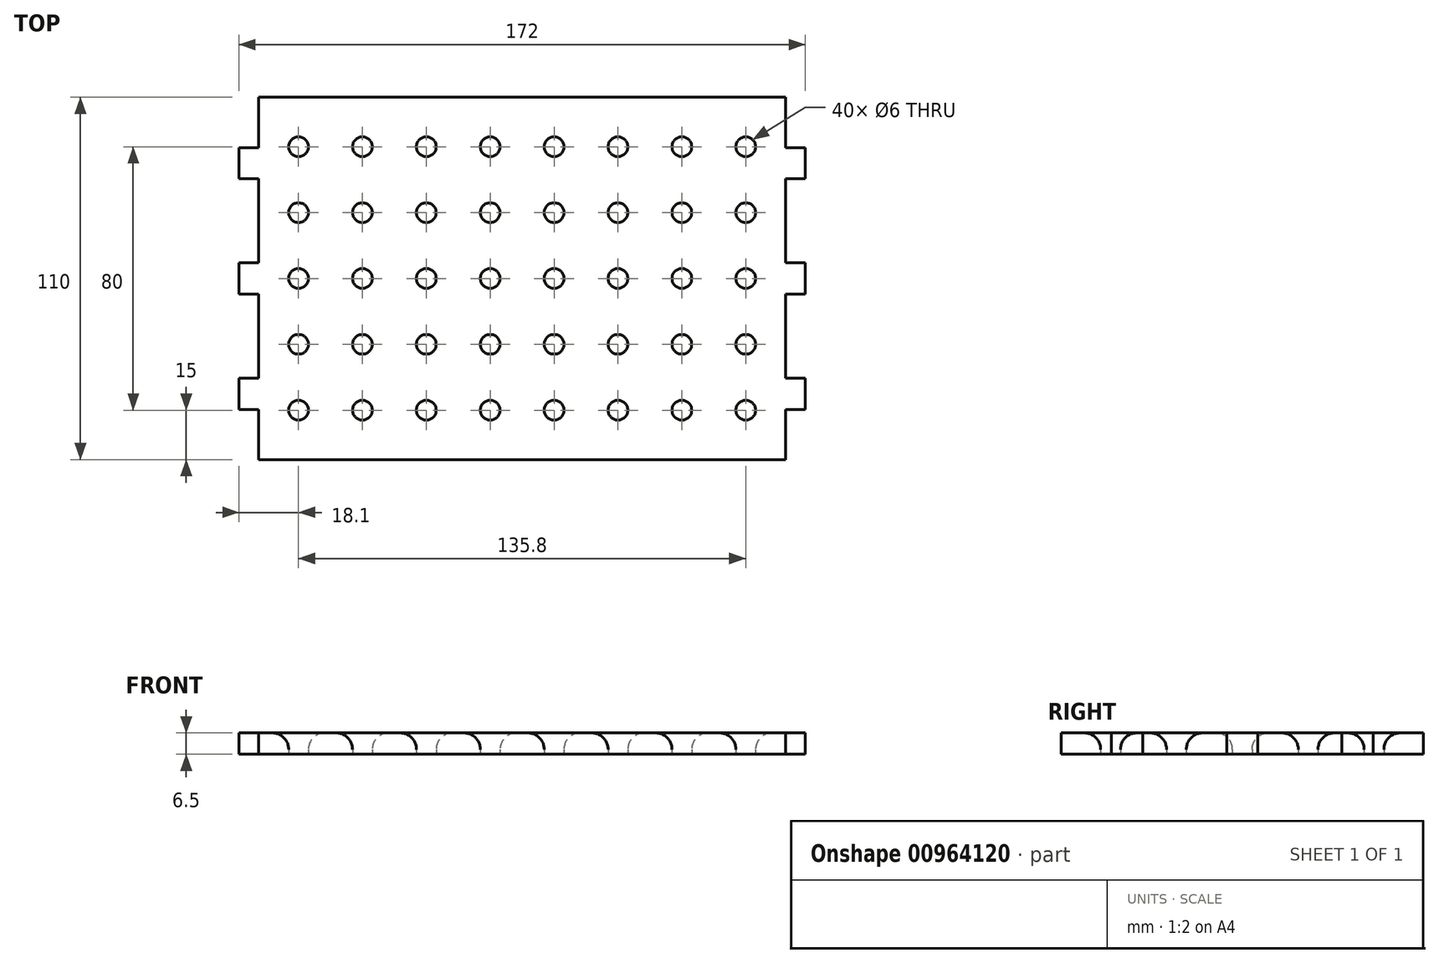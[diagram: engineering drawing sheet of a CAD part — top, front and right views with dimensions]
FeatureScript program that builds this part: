
annotation { "Feature Type Name" : "Feature", "Feature Type Description" : "" }
export const myFeature = defineFeature(function(context is Context, id is Id, definition is map)
    precondition{}
    {
        {
            var Q0;
            Q0=qCreatedBy(makeId("Top.planeOp"),FACE);
            var sketch = newSketch(context, id + "F0", { "sketchPlane" : qUnion([Q0])});
            skLineSegment(sketch, "E0.bottom", {"start": v(-80, 55) * mm, "end": v(80, 55) * mm});
            skLineSegment(sketch, "E0.top", {"start": v(-80, -55) * mm, "end": v(80, -55) * mm});
            skLineSegment(sketch, "E0.left", {"start": v(-80, 55) * mm, "end": v(-80, -55) * mm});
            skLineSegment(sketch, "E0.right", {"start": v(80, 55) * mm, "end": v(80, -55) * mm});
            skPoint(sketch, "E0.middle", {"position": v(0, 0) * mm});
            skSolve(sketch);
        }
        {
            var Q0;
            Q0=makeQuery(id+"F0.imprint","IMPRINT",FACE,{"disambiguationData":[TD([[makeQuery(id+"F0.imprint","IMPRINT",EDGE,{"derivedFrom":sQuery(id+"F0.wireOp",EDGE,"E0.bottom")}),-1.0]])]});
            extrude(context, id + "F1", {"entities" : qUnion([Q0]), "depth" : 6.5 * mm, "offsetDistance" : 25 * mm});
        }
        {
            var Q0;
            Q0=makeQuery(id+"F1.opExtrude","SWEPT_FACE",FACE,{"disambiguationData":[OSD([sQuery(id+"F0.wireOp",EDGE,"E0.left")])]});
            var sketch = newSketch(context, id + "F2", { "sketchPlane" : qUnion([Q0])});
            skLineSegment(sketch, "E1", {"start": v(-55, 3.25) * mm, "end": v(-35, 3.25) * mm});
            skLineSegment(sketch, "E2", {"start": v(-35, 3.25) * mm, "end": v(0, 3.25) * mm});
            skLineSegment(sketch, "E3", {"start": v(0, 3.25) * mm, "end": v(35, 3.25) * mm});
            skLineSegment(sketch, "E4", {"start": v(35, 3.25) * mm, "end": v(55, 3.25) * mm});
            skLineSegment(sketch, "E5.bottom", {"start": v(-39.75, 6.5) * mm, "end": v(-30.25, 6.5) * mm});
            skLineSegment(sketch, "E5.top", {"start": v(-39.75, 0) * mm, "end": v(-30.25, 0) * mm});
            skLineSegment(sketch, "E5.left", {"start": v(-39.75, 6.5) * mm, "end": v(-39.75, 0) * mm});
            skLineSegment(sketch, "E5.right", {"start": v(-30.25, 6.5) * mm, "end": v(-30.25, 0) * mm});
            skPoint(sketch, "E5.middle", {"position": v(-35, 3.25) * mm});
            skLineSegment(sketch, "E6.bottom", {"start": v(-4.75, 6.5) * mm, "end": v(4.75, 6.5) * mm});
            skLineSegment(sketch, "E6.top", {"start": v(-4.75, 0) * mm, "end": v(4.75, 0) * mm});
            skLineSegment(sketch, "E6.left", {"start": v(-4.75, 6.5) * mm, "end": v(-4.75, 0) * mm});
            skLineSegment(sketch, "E6.right", {"start": v(4.75, 6.5) * mm, "end": v(4.75, 0) * mm});
            skPoint(sketch, "E6.middle", {"position": v(0, 3.25) * mm});
            skLineSegment(sketch, "E7.bottom", {"start": v(39.75, 6.5) * mm, "end": v(30.25, 6.5) * mm});
            skLineSegment(sketch, "E7.top", {"start": v(39.75, 0) * mm, "end": v(30.25, 0) * mm});
            skLineSegment(sketch, "E7.left", {"start": v(39.75, 6.5) * mm, "end": v(39.75, 0) * mm});
            skLineSegment(sketch, "E7.right", {"start": v(30.25, 6.5) * mm, "end": v(30.25, 0) * mm});
            skPoint(sketch, "E7.middle", {"position": v(35, 3.25) * mm});
            skSolve(sketch);
        }
        {
            var Q0;
            {var subQ0=sQuery(id+"F2.wireOp",EDGE,"E5.bottom");Q0=makeQuery(id+"F2.imprint","IMPRINT",FACE,{"disambiguationData":[TD([[makeQuery(id+"F2.imprint","IMPRINT",EDGE,{"derivedFrom":subQ0}),-1.0]])]});}
            var Q1;
            {var subQ1=sQuery(id+"F2.wireOp",EDGE,"E5.top");Q1=makeQuery(id+"F2.imprint","IMPRINT",FACE,{"disambiguationData":[TD([[makeQuery(id+"F2.imprint","IMPRINT",EDGE,{"derivedFrom":subQ1}),1.0]])]});}
            var Q2;
            {var subQ1=sQuery(id+"F2.wireOp",EDGE,"E6.bottom");Q2=makeQuery(id+"F2.imprint","IMPRINT",FACE,{"disambiguationData":[TD([[makeQuery(id+"F2.imprint","IMPRINT",EDGE,{"derivedFrom":subQ1}),-1.0]])]});}
            var Q3;
            {var subQ0=sQuery(id+"F2.wireOp",EDGE,"E6.top");Q3=makeQuery(id+"F2.imprint","IMPRINT",FACE,{"disambiguationData":[TD([[makeQuery(id+"F2.imprint","IMPRINT",EDGE,{"derivedFrom":subQ0}),1.0]])]});}
            var Q4;
            {var subQ1=sQuery(id+"F2.wireOp",EDGE,"E7.bottom");Q4=makeQuery(id+"F2.imprint","IMPRINT",FACE,{"disambiguationData":[TD([[makeQuery(id+"F2.imprint","IMPRINT",EDGE,{"derivedFrom":subQ1}),-1.0]])]});}
            var Q5;
            {var subQ1=sQuery(id+"F2.wireOp",EDGE,"E7.top");Q5=makeQuery(id+"F2.imprint","IMPRINT",FACE,{"disambiguationData":[TD([[makeQuery(id+"F2.imprint","IMPRINT",EDGE,{"derivedFrom":subQ1}),1.0]])]});}
            extrude(context, id + "F3", {"entities" : qUnion([Q0, Q1, Q2, Q3, Q4, Q5]), "operationType" : NewBodyOperationType.ADD, "depth" : 6 * mm, "offsetDistance" : 25 * mm});
        }
        {
            var Q0;
            Q0=makeQuery(id+"F1.opExtrude","SWEPT_FACE",FACE,{"disambiguationData":[OSD([sQuery(id+"F0.wireOp",EDGE,"E0.right")])]});
            var sketch = newSketch(context, id + "F4", { "sketchPlane" : qUnion([Q0])});
            skLineSegment(sketch, "E8", {"start": v(-55, 3.25) * mm, "end": v(-35, 3.25) * mm});
            skLineSegment(sketch, "E9", {"start": v(-35, 3.25) * mm, "end": v(0, 3.25) * mm});
            skLineSegment(sketch, "E10", {"start": v(0, 3.25) * mm, "end": v(35, 3.25) * mm});
            skLineSegment(sketch, "E11.bottom", {"start": v(-39.75, 6.5) * mm, "end": v(-30.25, 6.5) * mm});
            skLineSegment(sketch, "E11.top", {"start": v(-39.75, 0) * mm, "end": v(-30.25, 0) * mm});
            skLineSegment(sketch, "E11.left", {"start": v(-39.75, 6.5) * mm, "end": v(-39.75, 0) * mm});
            skLineSegment(sketch, "E11.right", {"start": v(-30.25, 6.5) * mm, "end": v(-30.25, 0) * mm});
            skPoint(sketch, "E11.middle", {"position": v(-35, 3.25) * mm});
            skLineSegment(sketch, "E12.bottom", {"start": v(-4.75, 6.5) * mm, "end": v(4.75, 6.5) * mm});
            skLineSegment(sketch, "E12.top", {"start": v(-4.75, 0) * mm, "end": v(4.75, 0) * mm});
            skLineSegment(sketch, "E12.left", {"start": v(-4.75, 6.5) * mm, "end": v(-4.75, 0) * mm});
            skLineSegment(sketch, "E12.right", {"start": v(4.75, 6.5) * mm, "end": v(4.75, 0) * mm});
            skPoint(sketch, "E12.middle", {"position": v(0, 3.25) * mm});
            skLineSegment(sketch, "E13.bottom", {"start": v(39.75, 6.5) * mm, "end": v(30.25, 6.5) * mm});
            skLineSegment(sketch, "E13.top", {"start": v(39.75, 0) * mm, "end": v(30.25, 0) * mm});
            skLineSegment(sketch, "E13.left", {"start": v(39.75, 6.5) * mm, "end": v(39.75, 0) * mm});
            skLineSegment(sketch, "E13.right", {"start": v(30.25, 6.5) * mm, "end": v(30.25, 0) * mm});
            skPoint(sketch, "E13.middle", {"position": v(35, 3.25) * mm});
            skSolve(sketch);
        }
        {
            var Q0;
            {var subQ1=sQuery(id+"F4.wireOp",EDGE,"E11.bottom");Q0=makeQuery(id+"F4.imprint","IMPRINT",FACE,{"disambiguationData":[TD([[makeQuery(id+"F4.imprint","IMPRINT",EDGE,{"derivedFrom":subQ1}),1.0]])]});}
            var Q1;
            {var subQ1=sQuery(id+"F4.wireOp",EDGE,"E11.top");Q1=makeQuery(id+"F4.imprint","IMPRINT",FACE,{"disambiguationData":[TD([[makeQuery(id+"F4.imprint","IMPRINT",EDGE,{"derivedFrom":subQ1}),-1.0]])]});}
            var Q2;
            {var subQ0=sQuery(id+"F4.wireOp",EDGE,"E12.bottom");Q2=makeQuery(id+"F4.imprint","IMPRINT",FACE,{"disambiguationData":[TD([[makeQuery(id+"F4.imprint","IMPRINT",EDGE,{"derivedFrom":subQ0}),1.0]])]});}
            var Q3;
            {var subQ1=sQuery(id+"F4.wireOp",EDGE,"E12.top");Q3=makeQuery(id+"F4.imprint","IMPRINT",FACE,{"disambiguationData":[TD([[makeQuery(id+"F4.imprint","IMPRINT",EDGE,{"derivedFrom":subQ1}),-1.0]])]});}
            var Q4;
            {var subQ1=sQuery(id+"F4.wireOp",EDGE,"E13.bottom");Q4=makeQuery(id+"F4.imprint","IMPRINT",FACE,{"disambiguationData":[TD([[makeQuery(id+"F4.imprint","IMPRINT",EDGE,{"derivedFrom":subQ1}),1.0]])]});}
            extrude(context, id + "F5", {"entities" : qUnion([Q0, Q1, Q2, Q3, Q4]), "operationType" : NewBodyOperationType.ADD, "depth" : 6 * mm, "offsetDistance" : 25 * mm});
        }
        {
            var Q0;
            Q0=makeQuery(id+"F5.boolean.opBoolean","MERGE",FACE,{"derivedFrom":[makeQuery(id+"F3.boolean.opBoolean","MERGE",FACE,{"derivedFrom":[makeQuery(id+"F1.opExtrude","CAP_FACE",FACE,{"disambiguationData":[OSD([sQuery(id+"F0.wireOp",EDGE,"E0.bottom"),sQuery(id+"F0.wireOp",EDGE,"E0.top"),sQuery(id+"F0.wireOp",EDGE,"E0.left"),sQuery(id+"F0.wireOp",EDGE,"E0.right")])],"isStart":true}),makeQuery(id+"F3.opExtrude","SWEPT_FACE",FACE,{"disambiguationData":[OSD([sQuery(id+"F2.wireOp",EDGE,"E5.top")])]}),makeQuery(id+"F3.opExtrude","SWEPT_FACE",FACE,{"disambiguationData":[OSD([sQuery(id+"F2.wireOp",EDGE,"E6.top")])]}),makeQuery(id+"F3.opExtrude","SWEPT_FACE",FACE,{"disambiguationData":[OSD([sQuery(id+"F2.wireOp",EDGE,"E7.top")])]})]}),makeQuery(id+"F5.opExtrude","SWEPT_FACE",FACE,{"disambiguationData":[OSD([sQuery(id+"F4.wireOp",EDGE,"E11.top")])]}),makeQuery(id+"F5.opExtrude","SWEPT_FACE",FACE,{"disambiguationData":[OSD([sQuery(id+"F4.wireOp",EDGE,"E12.top")])]}),makeQuery(id+"F5.opExtrude","SWEPT_FACE",FACE,{"disambiguationData":[OSD([sQuery(id+"F4.wireOp",EDGE,"E13.top")])]})]});
            var sketch = newSketch(context, id + "F6", { "sketchPlane" : qUnion([Q0])});
            skCircle(sketch, "E14", {"center": v(-67.9, 40) * mm, "radius": 3 * mm});
            skCircle(sketch, "E15", {"center": v(-67.9, 20) * mm, "radius": 3 * mm});
            skCircle(sketch, "E16", {"center": v(-67.9, 0) * mm, "radius": 3 * mm});
            skCircle(sketch, "E17", {"center": v(-67.9, -20) * mm, "radius": 3 * mm});
            skCircle(sketch, "E18", {"center": v(-67.9, -40) * mm, "radius": 3 * mm});
            skCircle(sketch, "E19.1.0.0", {"center": v(-48.5, 40) * mm, "radius": 3 * mm});
            skCircle(sketch, "E19.1.0.1", {"center": v(-48.5, 20) * mm, "radius": 3 * mm});
            skCircle(sketch, "E19.1.0.2", {"center": v(-48.5, 0) * mm, "radius": 3 * mm});
            skCircle(sketch, "E19.1.0.3", {"center": v(-48.5, -20) * mm, "radius": 3 * mm});
            skCircle(sketch, "E19.1.0.4", {"center": v(-48.5, -40) * mm, "radius": 3 * mm});
            skCircle(sketch, "E19.2.0.0", {"center": v(-29.1, 40) * mm, "radius": 3 * mm});
            skCircle(sketch, "E19.2.0.1", {"center": v(-29.1, 20) * mm, "radius": 3 * mm});
            skCircle(sketch, "E19.2.0.2", {"center": v(-29.1, 0) * mm, "radius": 3 * mm});
            skCircle(sketch, "E19.2.0.3", {"center": v(-29.1, -20) * mm, "radius": 3 * mm});
            skCircle(sketch, "E19.2.0.4", {"center": v(-29.1, -40) * mm, "radius": 3 * mm});
            skCircle(sketch, "E19.3.0.0", {"center": v(-9.7, 40) * mm, "radius": 3 * mm});
            skCircle(sketch, "E19.3.0.1", {"center": v(-9.7, 20) * mm, "radius": 3 * mm});
            skCircle(sketch, "E19.3.0.2", {"center": v(-9.7, 0) * mm, "radius": 3 * mm});
            skCircle(sketch, "E19.3.0.3", {"center": v(-9.7, -20) * mm, "radius": 3 * mm});
            skCircle(sketch, "E19.3.0.4", {"center": v(-9.7, -40) * mm, "radius": 3 * mm});
            skCircle(sketch, "E19.4.0.0", {"center": v(9.7, 40) * mm, "radius": 3 * mm});
            skCircle(sketch, "E19.4.0.1", {"center": v(9.7, 20) * mm, "radius": 3 * mm});
            skCircle(sketch, "E19.4.0.2", {"center": v(9.7, 0) * mm, "radius": 3 * mm});
            skCircle(sketch, "E19.4.0.3", {"center": v(9.7, -20) * mm, "radius": 3 * mm});
            skCircle(sketch, "E19.4.0.4", {"center": v(9.7, -40) * mm, "radius": 3 * mm});
            skCircle(sketch, "E19.5.0.0", {"center": v(29.1, 40) * mm, "radius": 3 * mm});
            skCircle(sketch, "E19.5.0.1", {"center": v(29.1, 20) * mm, "radius": 3 * mm});
            skCircle(sketch, "E19.5.0.2", {"center": v(29.1, 0) * mm, "radius": 3 * mm});
            skCircle(sketch, "E19.5.0.3", {"center": v(29.1, -20) * mm, "radius": 3 * mm});
            skCircle(sketch, "E19.5.0.4", {"center": v(29.1, -40) * mm, "radius": 3 * mm});
            skCircle(sketch, "E19.6.0.0", {"center": v(48.5, 40) * mm, "radius": 3 * mm});
            skCircle(sketch, "E19.6.0.1", {"center": v(48.5, 20) * mm, "radius": 3 * mm});
            skCircle(sketch, "E19.6.0.2", {"center": v(48.5, 0) * mm, "radius": 3 * mm});
            skCircle(sketch, "E19.6.0.3", {"center": v(48.5, -20) * mm, "radius": 3 * mm});
            skCircle(sketch, "E19.6.0.4", {"center": v(48.5, -40) * mm, "radius": 3 * mm});
            skCircle(sketch, "E19.7.0.0", {"center": v(67.9, 40) * mm, "radius": 3 * mm});
            skCircle(sketch, "E19.7.0.1", {"center": v(67.9, 20) * mm, "radius": 3 * mm});
            skCircle(sketch, "E19.7.0.2", {"center": v(67.9, 0) * mm, "radius": 3 * mm});
            skCircle(sketch, "E19.7.0.3", {"center": v(67.9, -20) * mm, "radius": 3 * mm});
            skCircle(sketch, "E19.7.0.4", {"center": v(67.9, -40) * mm, "radius": 3 * mm});
            skLineSegment(sketch, "E19.direction1", {"start": v(-67.9, 40) * mm, "end": v(-48.5, 40) * mm, "construction": true});
            skSolve(sketch);
        }
        {
            var Q0;
            Q0=makeQuery(id+"F6.imprint","IMPRINT",FACE,{"disambiguationData":[TD([[makeQuery(id+"F6.imprint","IMPRINT",EDGE,{"derivedFrom":sQuery(id+"F6.wireOp",EDGE,"E14")}),1.0]])]});
            var Q1;
            Q1=makeQuery(id+"F6.imprint","IMPRINT",FACE,{"disambiguationData":[TD([[makeQuery(id+"F6.imprint","IMPRINT",EDGE,{"derivedFrom":sQuery(id+"F6.wireOp",EDGE,"E19.1.0.0")}),1.0]])]});
            var Q2;
            Q2=makeQuery(id+"F6.imprint","IMPRINT",FACE,{"disambiguationData":[TD([[makeQuery(id+"F6.imprint","IMPRINT",EDGE,{"derivedFrom":sQuery(id+"F6.wireOp",EDGE,"E19.2.0.0")}),1.0]])]});
            var Q3;
            Q3=makeQuery(id+"F6.imprint","IMPRINT",FACE,{"disambiguationData":[TD([[makeQuery(id+"F6.imprint","IMPRINT",EDGE,{"derivedFrom":sQuery(id+"F6.wireOp",EDGE,"E19.3.0.0")}),1.0]])]});
            var Q4;
            Q4=makeQuery(id+"F6.imprint","IMPRINT",FACE,{"disambiguationData":[TD([[makeQuery(id+"F6.imprint","IMPRINT",EDGE,{"derivedFrom":sQuery(id+"F6.wireOp",EDGE,"E19.4.0.0")}),1.0]])]});
            var Q5;
            Q5=makeQuery(id+"F6.imprint","IMPRINT",FACE,{"disambiguationData":[TD([[makeQuery(id+"F6.imprint","IMPRINT",EDGE,{"derivedFrom":sQuery(id+"F6.wireOp",EDGE,"E19.5.0.0")}),1.0]])]});
            var Q6;
            Q6=makeQuery(id+"F6.imprint","IMPRINT",FACE,{"disambiguationData":[TD([[makeQuery(id+"F6.imprint","IMPRINT",EDGE,{"derivedFrom":sQuery(id+"F6.wireOp",EDGE,"E19.6.0.0")}),1.0]])]});
            var Q7;
            Q7=makeQuery(id+"F6.imprint","IMPRINT",FACE,{"disambiguationData":[TD([[makeQuery(id+"F6.imprint","IMPRINT",EDGE,{"derivedFrom":sQuery(id+"F6.wireOp",EDGE,"E19.7.0.0")}),1.0]])]});
            var Q8;
            Q8=makeQuery(id+"F6.imprint","IMPRINT",FACE,{"disambiguationData":[TD([[makeQuery(id+"F6.imprint","IMPRINT",EDGE,{"derivedFrom":sQuery(id+"F6.wireOp",EDGE,"E19.7.0.1")}),1.0]])]});
            var Q9;
            Q9=makeQuery(id+"F6.imprint","IMPRINT",FACE,{"disambiguationData":[TD([[makeQuery(id+"F6.imprint","IMPRINT",EDGE,{"derivedFrom":sQuery(id+"F6.wireOp",EDGE,"E19.6.0.1")}),1.0]])]});
            var Q10;
            Q10=makeQuery(id+"F6.imprint","IMPRINT",FACE,{"disambiguationData":[TD([[makeQuery(id+"F6.imprint","IMPRINT",EDGE,{"derivedFrom":sQuery(id+"F6.wireOp",EDGE,"E19.5.0.1")}),1.0]])]});
            var Q11;
            Q11=makeQuery(id+"F6.imprint","IMPRINT",FACE,{"disambiguationData":[TD([[makeQuery(id+"F6.imprint","IMPRINT",EDGE,{"derivedFrom":sQuery(id+"F6.wireOp",EDGE,"E19.4.0.1")}),1.0]])]});
            var Q12;
            Q12=makeQuery(id+"F6.imprint","IMPRINT",FACE,{"disambiguationData":[TD([[makeQuery(id+"F6.imprint","IMPRINT",EDGE,{"derivedFrom":sQuery(id+"F6.wireOp",EDGE,"E19.3.0.1")}),1.0]])]});
            var Q13;
            Q13=makeQuery(id+"F6.imprint","IMPRINT",FACE,{"disambiguationData":[TD([[makeQuery(id+"F6.imprint","IMPRINT",EDGE,{"derivedFrom":sQuery(id+"F6.wireOp",EDGE,"E19.2.0.1")}),1.0]])]});
            var Q14;
            Q14=makeQuery(id+"F6.imprint","IMPRINT",FACE,{"disambiguationData":[TD([[makeQuery(id+"F6.imprint","IMPRINT",EDGE,{"derivedFrom":sQuery(id+"F6.wireOp",EDGE,"E19.1.0.1")}),1.0]])]});
            var Q15;
            Q15=makeQuery(id+"F6.imprint","IMPRINT",FACE,{"disambiguationData":[TD([[makeQuery(id+"F6.imprint","IMPRINT",EDGE,{"derivedFrom":sQuery(id+"F6.wireOp",EDGE,"E15")}),1.0]])]});
            var Q16;
            Q16=makeQuery(id+"F6.imprint","IMPRINT",FACE,{"disambiguationData":[TD([[makeQuery(id+"F6.imprint","IMPRINT",EDGE,{"derivedFrom":sQuery(id+"F6.wireOp",EDGE,"E16")}),1.0]])]});
            var Q17;
            Q17=makeQuery(id+"F6.imprint","IMPRINT",FACE,{"disambiguationData":[TD([[makeQuery(id+"F6.imprint","IMPRINT",EDGE,{"derivedFrom":sQuery(id+"F6.wireOp",EDGE,"E19.1.0.2")}),1.0]])]});
            var Q18;
            Q18=makeQuery(id+"F6.imprint","IMPRINT",FACE,{"disambiguationData":[TD([[makeQuery(id+"F6.imprint","IMPRINT",EDGE,{"derivedFrom":sQuery(id+"F6.wireOp",EDGE,"E19.2.0.2")}),1.0]])]});
            var Q19;
            Q19=makeQuery(id+"F6.imprint","IMPRINT",FACE,{"disambiguationData":[TD([[makeQuery(id+"F6.imprint","IMPRINT",EDGE,{"derivedFrom":sQuery(id+"F6.wireOp",EDGE,"E19.3.0.2")}),1.0]])]});
            var Q20;
            Q20=makeQuery(id+"F6.imprint","IMPRINT",FACE,{"disambiguationData":[TD([[makeQuery(id+"F6.imprint","IMPRINT",EDGE,{"derivedFrom":sQuery(id+"F6.wireOp",EDGE,"E19.4.0.2")}),1.0]])]});
            var Q21;
            Q21=makeQuery(id+"F6.imprint","IMPRINT",FACE,{"disambiguationData":[TD([[makeQuery(id+"F6.imprint","IMPRINT",EDGE,{"derivedFrom":sQuery(id+"F6.wireOp",EDGE,"E19.5.0.2")}),1.0]])]});
            var Q22;
            Q22=makeQuery(id+"F6.imprint","IMPRINT",FACE,{"disambiguationData":[TD([[makeQuery(id+"F6.imprint","IMPRINT",EDGE,{"derivedFrom":sQuery(id+"F6.wireOp",EDGE,"E19.6.0.2")}),1.0]])]});
            var Q23;
            Q23=makeQuery(id+"F6.imprint","IMPRINT",FACE,{"disambiguationData":[TD([[makeQuery(id+"F6.imprint","IMPRINT",EDGE,{"derivedFrom":sQuery(id+"F6.wireOp",EDGE,"E19.7.0.2")}),1.0]])]});
            var Q24;
            Q24=makeQuery(id+"F6.imprint","IMPRINT",FACE,{"disambiguationData":[TD([[makeQuery(id+"F6.imprint","IMPRINT",EDGE,{"derivedFrom":sQuery(id+"F6.wireOp",EDGE,"E19.7.0.3")}),1.0]])]});
            var Q25;
            Q25=makeQuery(id+"F6.imprint","IMPRINT",FACE,{"disambiguationData":[TD([[makeQuery(id+"F6.imprint","IMPRINT",EDGE,{"derivedFrom":sQuery(id+"F6.wireOp",EDGE,"E19.6.0.3")}),1.0]])]});
            var Q26;
            Q26=makeQuery(id+"F6.imprint","IMPRINT",FACE,{"disambiguationData":[TD([[makeQuery(id+"F6.imprint","IMPRINT",EDGE,{"derivedFrom":sQuery(id+"F6.wireOp",EDGE,"E19.5.0.3")}),1.0]])]});
            var Q27;
            Q27=makeQuery(id+"F6.imprint","IMPRINT",FACE,{"disambiguationData":[TD([[makeQuery(id+"F6.imprint","IMPRINT",EDGE,{"derivedFrom":sQuery(id+"F6.wireOp",EDGE,"E19.4.0.3")}),1.0]])]});
            var Q28;
            Q28=makeQuery(id+"F6.imprint","IMPRINT",FACE,{"disambiguationData":[TD([[makeQuery(id+"F6.imprint","IMPRINT",EDGE,{"derivedFrom":sQuery(id+"F6.wireOp",EDGE,"E19.3.0.3")}),1.0]])]});
            var Q29;
            Q29=makeQuery(id+"F6.imprint","IMPRINT",FACE,{"disambiguationData":[TD([[makeQuery(id+"F6.imprint","IMPRINT",EDGE,{"derivedFrom":sQuery(id+"F6.wireOp",EDGE,"E19.2.0.3")}),1.0]])]});
            var Q30;
            Q30=makeQuery(id+"F6.imprint","IMPRINT",FACE,{"disambiguationData":[TD([[makeQuery(id+"F6.imprint","IMPRINT",EDGE,{"derivedFrom":sQuery(id+"F6.wireOp",EDGE,"E19.1.0.3")}),1.0]])]});
            var Q31;
            Q31=makeQuery(id+"F6.imprint","IMPRINT",FACE,{"disambiguationData":[TD([[makeQuery(id+"F6.imprint","IMPRINT",EDGE,{"derivedFrom":sQuery(id+"F6.wireOp",EDGE,"E17")}),1.0]])]});
            var Q32;
            Q32=makeQuery(id+"F6.imprint","IMPRINT",FACE,{"disambiguationData":[TD([[makeQuery(id+"F6.imprint","IMPRINT",EDGE,{"derivedFrom":sQuery(id+"F6.wireOp",EDGE,"E18")}),1.0]])]});
            var Q33;
            Q33=makeQuery(id+"F6.imprint","IMPRINT",FACE,{"disambiguationData":[TD([[makeQuery(id+"F6.imprint","IMPRINT",EDGE,{"derivedFrom":sQuery(id+"F6.wireOp",EDGE,"E19.1.0.4")}),1.0]])]});
            var Q34;
            Q34=makeQuery(id+"F6.imprint","IMPRINT",FACE,{"disambiguationData":[TD([[makeQuery(id+"F6.imprint","IMPRINT",EDGE,{"derivedFrom":sQuery(id+"F6.wireOp",EDGE,"E19.2.0.4")}),1.0]])]});
            var Q35;
            Q35=makeQuery(id+"F6.imprint","IMPRINT",FACE,{"disambiguationData":[TD([[makeQuery(id+"F6.imprint","IMPRINT",EDGE,{"derivedFrom":sQuery(id+"F6.wireOp",EDGE,"E19.3.0.4")}),1.0]])]});
            var Q36;
            Q36=makeQuery(id+"F6.imprint","IMPRINT",FACE,{"disambiguationData":[TD([[makeQuery(id+"F6.imprint","IMPRINT",EDGE,{"derivedFrom":sQuery(id+"F6.wireOp",EDGE,"E19.4.0.4")}),1.0]])]});
            var Q37;
            Q37=makeQuery(id+"F6.imprint","IMPRINT",FACE,{"disambiguationData":[TD([[makeQuery(id+"F6.imprint","IMPRINT",EDGE,{"derivedFrom":sQuery(id+"F6.wireOp",EDGE,"E19.5.0.4")}),1.0]])]});
            var Q38;
            Q38=makeQuery(id+"F6.imprint","IMPRINT",FACE,{"disambiguationData":[TD([[makeQuery(id+"F6.imprint","IMPRINT",EDGE,{"derivedFrom":sQuery(id+"F6.wireOp",EDGE,"E19.6.0.4")}),1.0]])]});
            var Q39;
            Q39=makeQuery(id+"F6.imprint","IMPRINT",FACE,{"disambiguationData":[TD([[makeQuery(id+"F6.imprint","IMPRINT",EDGE,{"derivedFrom":sQuery(id+"F6.wireOp",EDGE,"E19.7.0.4")}),1.0]])]});
            extrude(context, id + "F7", {"entities" : qUnion([Q0, Q1, Q2, Q3, Q4, Q5, Q6, Q7, Q8, Q9, Q10, Q11, Q12, Q13, Q14, Q15, Q16, Q17, Q18, Q19, Q20, Q21, Q22, Q23, Q24, Q25, Q26, Q27, Q28, Q29, Q30, Q31, Q32, Q33, Q34, Q35, Q36, Q37, Q38, Q39]), "operationType" : NewBodyOperationType.REMOVE, "oppositeDirection" : true, "depth" : 25 * mm, "offsetDistance" : 25 * mm});
        }
        {
            var Q0;
            Q0=makeQuery(id+"F7.boolean.opBoolean","INTERSECT",EDGE,{"derivedFrom":[makeQuery(id+"F5.boolean.opBoolean","MERGE",FACE,{"derivedFrom":[makeQuery(id+"F3.boolean.opBoolean","MERGE",FACE,{"derivedFrom":[makeQuery(id+"F1.opExtrude","CAP_FACE",FACE,{"disambiguationData":[OSD([sQuery(id+"F0.wireOp",EDGE,"E0.bottom"),sQuery(id+"F0.wireOp",EDGE,"E0.top"),sQuery(id+"F0.wireOp",EDGE,"E0.left"),sQuery(id+"F0.wireOp",EDGE,"E0.right")])],"isStart":false}),makeQuery(id+"F3.opExtrude","SWEPT_FACE",FACE,{"disambiguationData":[OSD([sQuery(id+"F2.wireOp",EDGE,"E5.bottom")])]}),makeQuery(id+"F3.opExtrude","SWEPT_FACE",FACE,{"disambiguationData":[OSD([sQuery(id+"F2.wireOp",EDGE,"E6.bottom")])]}),makeQuery(id+"F3.opExtrude","SWEPT_FACE",FACE,{"disambiguationData":[OSD([sQuery(id+"F2.wireOp",EDGE,"E7.bottom")])]})]}),makeQuery(id+"F5.opExtrude","SWEPT_FACE",FACE,{"disambiguationData":[OSD([sQuery(id+"F4.wireOp",EDGE,"E11.bottom")])]}),makeQuery(id+"F5.opExtrude","SWEPT_FACE",FACE,{"disambiguationData":[OSD([sQuery(id+"F4.wireOp",EDGE,"E12.bottom")])]}),makeQuery(id+"F5.opExtrude","SWEPT_FACE",FACE,{"disambiguationData":[OSD([sQuery(id+"F4.wireOp",EDGE,"E13.bottom")])]})]}),makeQuery(id+"F7.opExtrude","SWEPT_FACE",FACE,{"disambiguationData":[OSD([sQuery(id+"F6.wireOp",EDGE,"E18")])]})]});
            var Q1;
            Q1=makeQuery(id+"F7.boolean.opBoolean","INTERSECT",EDGE,{"derivedFrom":[makeQuery(id+"F5.boolean.opBoolean","MERGE",FACE,{"derivedFrom":[makeQuery(id+"F3.boolean.opBoolean","MERGE",FACE,{"derivedFrom":[makeQuery(id+"F1.opExtrude","CAP_FACE",FACE,{"disambiguationData":[OSD([sQuery(id+"F0.wireOp",EDGE,"E0.bottom"),sQuery(id+"F0.wireOp",EDGE,"E0.top"),sQuery(id+"F0.wireOp",EDGE,"E0.left"),sQuery(id+"F0.wireOp",EDGE,"E0.right")])],"isStart":false}),makeQuery(id+"F3.opExtrude","SWEPT_FACE",FACE,{"disambiguationData":[OSD([sQuery(id+"F2.wireOp",EDGE,"E5.bottom")])]}),makeQuery(id+"F3.opExtrude","SWEPT_FACE",FACE,{"disambiguationData":[OSD([sQuery(id+"F2.wireOp",EDGE,"E6.bottom")])]}),makeQuery(id+"F3.opExtrude","SWEPT_FACE",FACE,{"disambiguationData":[OSD([sQuery(id+"F2.wireOp",EDGE,"E7.bottom")])]})]}),makeQuery(id+"F5.opExtrude","SWEPT_FACE",FACE,{"disambiguationData":[OSD([sQuery(id+"F4.wireOp",EDGE,"E11.bottom")])]}),makeQuery(id+"F5.opExtrude","SWEPT_FACE",FACE,{"disambiguationData":[OSD([sQuery(id+"F4.wireOp",EDGE,"E12.bottom")])]}),makeQuery(id+"F5.opExtrude","SWEPT_FACE",FACE,{"disambiguationData":[OSD([sQuery(id+"F4.wireOp",EDGE,"E13.bottom")])]})]}),makeQuery(id+"F7.opExtrude","SWEPT_FACE",FACE,{"disambiguationData":[OSD([sQuery(id+"F6.wireOp",EDGE,"E19.1.0.4")])]})]});
            var Q2;
            Q2=makeQuery(id+"F7.boolean.opBoolean","INTERSECT",EDGE,{"derivedFrom":[makeQuery(id+"F5.boolean.opBoolean","MERGE",FACE,{"derivedFrom":[makeQuery(id+"F3.boolean.opBoolean","MERGE",FACE,{"derivedFrom":[makeQuery(id+"F1.opExtrude","CAP_FACE",FACE,{"disambiguationData":[OSD([sQuery(id+"F0.wireOp",EDGE,"E0.bottom"),sQuery(id+"F0.wireOp",EDGE,"E0.top"),sQuery(id+"F0.wireOp",EDGE,"E0.left"),sQuery(id+"F0.wireOp",EDGE,"E0.right")])],"isStart":false}),makeQuery(id+"F3.opExtrude","SWEPT_FACE",FACE,{"disambiguationData":[OSD([sQuery(id+"F2.wireOp",EDGE,"E5.bottom")])]}),makeQuery(id+"F3.opExtrude","SWEPT_FACE",FACE,{"disambiguationData":[OSD([sQuery(id+"F2.wireOp",EDGE,"E6.bottom")])]}),makeQuery(id+"F3.opExtrude","SWEPT_FACE",FACE,{"disambiguationData":[OSD([sQuery(id+"F2.wireOp",EDGE,"E7.bottom")])]})]}),makeQuery(id+"F5.opExtrude","SWEPT_FACE",FACE,{"disambiguationData":[OSD([sQuery(id+"F4.wireOp",EDGE,"E11.bottom")])]}),makeQuery(id+"F5.opExtrude","SWEPT_FACE",FACE,{"disambiguationData":[OSD([sQuery(id+"F4.wireOp",EDGE,"E12.bottom")])]}),makeQuery(id+"F5.opExtrude","SWEPT_FACE",FACE,{"disambiguationData":[OSD([sQuery(id+"F4.wireOp",EDGE,"E13.bottom")])]})]}),makeQuery(id+"F7.opExtrude","SWEPT_FACE",FACE,{"disambiguationData":[OSD([sQuery(id+"F6.wireOp",EDGE,"E19.2.0.4")])]})]});
            var Q3;
            Q3=makeQuery(id+"F7.boolean.opBoolean","INTERSECT",EDGE,{"derivedFrom":[makeQuery(id+"F5.boolean.opBoolean","MERGE",FACE,{"derivedFrom":[makeQuery(id+"F3.boolean.opBoolean","MERGE",FACE,{"derivedFrom":[makeQuery(id+"F1.opExtrude","CAP_FACE",FACE,{"disambiguationData":[OSD([sQuery(id+"F0.wireOp",EDGE,"E0.bottom"),sQuery(id+"F0.wireOp",EDGE,"E0.top"),sQuery(id+"F0.wireOp",EDGE,"E0.left"),sQuery(id+"F0.wireOp",EDGE,"E0.right")])],"isStart":false}),makeQuery(id+"F3.opExtrude","SWEPT_FACE",FACE,{"disambiguationData":[OSD([sQuery(id+"F2.wireOp",EDGE,"E5.bottom")])]}),makeQuery(id+"F3.opExtrude","SWEPT_FACE",FACE,{"disambiguationData":[OSD([sQuery(id+"F2.wireOp",EDGE,"E6.bottom")])]}),makeQuery(id+"F3.opExtrude","SWEPT_FACE",FACE,{"disambiguationData":[OSD([sQuery(id+"F2.wireOp",EDGE,"E7.bottom")])]})]}),makeQuery(id+"F5.opExtrude","SWEPT_FACE",FACE,{"disambiguationData":[OSD([sQuery(id+"F4.wireOp",EDGE,"E11.bottom")])]}),makeQuery(id+"F5.opExtrude","SWEPT_FACE",FACE,{"disambiguationData":[OSD([sQuery(id+"F4.wireOp",EDGE,"E12.bottom")])]}),makeQuery(id+"F5.opExtrude","SWEPT_FACE",FACE,{"disambiguationData":[OSD([sQuery(id+"F4.wireOp",EDGE,"E13.bottom")])]})]}),makeQuery(id+"F7.opExtrude","SWEPT_FACE",FACE,{"disambiguationData":[OSD([sQuery(id+"F6.wireOp",EDGE,"E19.3.0.4")])]})]});
            var Q4;
            Q4=makeQuery(id+"F7.boolean.opBoolean","INTERSECT",EDGE,{"derivedFrom":[makeQuery(id+"F5.boolean.opBoolean","MERGE",FACE,{"derivedFrom":[makeQuery(id+"F3.boolean.opBoolean","MERGE",FACE,{"derivedFrom":[makeQuery(id+"F1.opExtrude","CAP_FACE",FACE,{"disambiguationData":[OSD([sQuery(id+"F0.wireOp",EDGE,"E0.bottom"),sQuery(id+"F0.wireOp",EDGE,"E0.top"),sQuery(id+"F0.wireOp",EDGE,"E0.left"),sQuery(id+"F0.wireOp",EDGE,"E0.right")])],"isStart":false}),makeQuery(id+"F3.opExtrude","SWEPT_FACE",FACE,{"disambiguationData":[OSD([sQuery(id+"F2.wireOp",EDGE,"E5.bottom")])]}),makeQuery(id+"F3.opExtrude","SWEPT_FACE",FACE,{"disambiguationData":[OSD([sQuery(id+"F2.wireOp",EDGE,"E6.bottom")])]}),makeQuery(id+"F3.opExtrude","SWEPT_FACE",FACE,{"disambiguationData":[OSD([sQuery(id+"F2.wireOp",EDGE,"E7.bottom")])]})]}),makeQuery(id+"F5.opExtrude","SWEPT_FACE",FACE,{"disambiguationData":[OSD([sQuery(id+"F4.wireOp",EDGE,"E11.bottom")])]}),makeQuery(id+"F5.opExtrude","SWEPT_FACE",FACE,{"disambiguationData":[OSD([sQuery(id+"F4.wireOp",EDGE,"E12.bottom")])]}),makeQuery(id+"F5.opExtrude","SWEPT_FACE",FACE,{"disambiguationData":[OSD([sQuery(id+"F4.wireOp",EDGE,"E13.bottom")])]})]}),makeQuery(id+"F7.opExtrude","SWEPT_FACE",FACE,{"disambiguationData":[OSD([sQuery(id+"F6.wireOp",EDGE,"E19.4.0.4")])]})]});
            var Q5;
            Q5=makeQuery(id+"F7.boolean.opBoolean","INTERSECT",EDGE,{"derivedFrom":[makeQuery(id+"F5.boolean.opBoolean","MERGE",FACE,{"derivedFrom":[makeQuery(id+"F3.boolean.opBoolean","MERGE",FACE,{"derivedFrom":[makeQuery(id+"F1.opExtrude","CAP_FACE",FACE,{"disambiguationData":[OSD([sQuery(id+"F0.wireOp",EDGE,"E0.bottom"),sQuery(id+"F0.wireOp",EDGE,"E0.top"),sQuery(id+"F0.wireOp",EDGE,"E0.left"),sQuery(id+"F0.wireOp",EDGE,"E0.right")])],"isStart":false}),makeQuery(id+"F3.opExtrude","SWEPT_FACE",FACE,{"disambiguationData":[OSD([sQuery(id+"F2.wireOp",EDGE,"E5.bottom")])]}),makeQuery(id+"F3.opExtrude","SWEPT_FACE",FACE,{"disambiguationData":[OSD([sQuery(id+"F2.wireOp",EDGE,"E6.bottom")])]}),makeQuery(id+"F3.opExtrude","SWEPT_FACE",FACE,{"disambiguationData":[OSD([sQuery(id+"F2.wireOp",EDGE,"E7.bottom")])]})]}),makeQuery(id+"F5.opExtrude","SWEPT_FACE",FACE,{"disambiguationData":[OSD([sQuery(id+"F4.wireOp",EDGE,"E11.bottom")])]}),makeQuery(id+"F5.opExtrude","SWEPT_FACE",FACE,{"disambiguationData":[OSD([sQuery(id+"F4.wireOp",EDGE,"E12.bottom")])]}),makeQuery(id+"F5.opExtrude","SWEPT_FACE",FACE,{"disambiguationData":[OSD([sQuery(id+"F4.wireOp",EDGE,"E13.bottom")])]})]}),makeQuery(id+"F7.opExtrude","SWEPT_FACE",FACE,{"disambiguationData":[OSD([sQuery(id+"F6.wireOp",EDGE,"E19.5.0.4")])]})]});
            var Q6;
            Q6=makeQuery(id+"F7.boolean.opBoolean","INTERSECT",EDGE,{"derivedFrom":[makeQuery(id+"F5.boolean.opBoolean","MERGE",FACE,{"derivedFrom":[makeQuery(id+"F3.boolean.opBoolean","MERGE",FACE,{"derivedFrom":[makeQuery(id+"F1.opExtrude","CAP_FACE",FACE,{"disambiguationData":[OSD([sQuery(id+"F0.wireOp",EDGE,"E0.bottom"),sQuery(id+"F0.wireOp",EDGE,"E0.top"),sQuery(id+"F0.wireOp",EDGE,"E0.left"),sQuery(id+"F0.wireOp",EDGE,"E0.right")])],"isStart":false}),makeQuery(id+"F3.opExtrude","SWEPT_FACE",FACE,{"disambiguationData":[OSD([sQuery(id+"F2.wireOp",EDGE,"E5.bottom")])]}),makeQuery(id+"F3.opExtrude","SWEPT_FACE",FACE,{"disambiguationData":[OSD([sQuery(id+"F2.wireOp",EDGE,"E6.bottom")])]}),makeQuery(id+"F3.opExtrude","SWEPT_FACE",FACE,{"disambiguationData":[OSD([sQuery(id+"F2.wireOp",EDGE,"E7.bottom")])]})]}),makeQuery(id+"F5.opExtrude","SWEPT_FACE",FACE,{"disambiguationData":[OSD([sQuery(id+"F4.wireOp",EDGE,"E11.bottom")])]}),makeQuery(id+"F5.opExtrude","SWEPT_FACE",FACE,{"disambiguationData":[OSD([sQuery(id+"F4.wireOp",EDGE,"E12.bottom")])]}),makeQuery(id+"F5.opExtrude","SWEPT_FACE",FACE,{"disambiguationData":[OSD([sQuery(id+"F4.wireOp",EDGE,"E13.bottom")])]})]}),makeQuery(id+"F7.opExtrude","SWEPT_FACE",FACE,{"disambiguationData":[OSD([sQuery(id+"F6.wireOp",EDGE,"E19.6.0.4")])]})]});
            var Q7;
            Q7=makeQuery(id+"F7.boolean.opBoolean","INTERSECT",EDGE,{"derivedFrom":[makeQuery(id+"F5.boolean.opBoolean","MERGE",FACE,{"derivedFrom":[makeQuery(id+"F3.boolean.opBoolean","MERGE",FACE,{"derivedFrom":[makeQuery(id+"F1.opExtrude","CAP_FACE",FACE,{"disambiguationData":[OSD([sQuery(id+"F0.wireOp",EDGE,"E0.bottom"),sQuery(id+"F0.wireOp",EDGE,"E0.top"),sQuery(id+"F0.wireOp",EDGE,"E0.left"),sQuery(id+"F0.wireOp",EDGE,"E0.right")])],"isStart":false}),makeQuery(id+"F3.opExtrude","SWEPT_FACE",FACE,{"disambiguationData":[OSD([sQuery(id+"F2.wireOp",EDGE,"E5.bottom")])]}),makeQuery(id+"F3.opExtrude","SWEPT_FACE",FACE,{"disambiguationData":[OSD([sQuery(id+"F2.wireOp",EDGE,"E6.bottom")])]}),makeQuery(id+"F3.opExtrude","SWEPT_FACE",FACE,{"disambiguationData":[OSD([sQuery(id+"F2.wireOp",EDGE,"E7.bottom")])]})]}),makeQuery(id+"F5.opExtrude","SWEPT_FACE",FACE,{"disambiguationData":[OSD([sQuery(id+"F4.wireOp",EDGE,"E11.bottom")])]}),makeQuery(id+"F5.opExtrude","SWEPT_FACE",FACE,{"disambiguationData":[OSD([sQuery(id+"F4.wireOp",EDGE,"E12.bottom")])]}),makeQuery(id+"F5.opExtrude","SWEPT_FACE",FACE,{"disambiguationData":[OSD([sQuery(id+"F4.wireOp",EDGE,"E13.bottom")])]})]}),makeQuery(id+"F7.opExtrude","SWEPT_FACE",FACE,{"disambiguationData":[OSD([sQuery(id+"F6.wireOp",EDGE,"E19.7.0.4")])]})]});
            var Q8;
            Q8=makeQuery(id+"F7.boolean.opBoolean","INTERSECT",EDGE,{"derivedFrom":[makeQuery(id+"F5.boolean.opBoolean","MERGE",FACE,{"derivedFrom":[makeQuery(id+"F3.boolean.opBoolean","MERGE",FACE,{"derivedFrom":[makeQuery(id+"F1.opExtrude","CAP_FACE",FACE,{"disambiguationData":[OSD([sQuery(id+"F0.wireOp",EDGE,"E0.bottom"),sQuery(id+"F0.wireOp",EDGE,"E0.top"),sQuery(id+"F0.wireOp",EDGE,"E0.left"),sQuery(id+"F0.wireOp",EDGE,"E0.right")])],"isStart":false}),makeQuery(id+"F3.opExtrude","SWEPT_FACE",FACE,{"disambiguationData":[OSD([sQuery(id+"F2.wireOp",EDGE,"E5.bottom")])]}),makeQuery(id+"F3.opExtrude","SWEPT_FACE",FACE,{"disambiguationData":[OSD([sQuery(id+"F2.wireOp",EDGE,"E6.bottom")])]}),makeQuery(id+"F3.opExtrude","SWEPT_FACE",FACE,{"disambiguationData":[OSD([sQuery(id+"F2.wireOp",EDGE,"E7.bottom")])]})]}),makeQuery(id+"F5.opExtrude","SWEPT_FACE",FACE,{"disambiguationData":[OSD([sQuery(id+"F4.wireOp",EDGE,"E11.bottom")])]}),makeQuery(id+"F5.opExtrude","SWEPT_FACE",FACE,{"disambiguationData":[OSD([sQuery(id+"F4.wireOp",EDGE,"E12.bottom")])]}),makeQuery(id+"F5.opExtrude","SWEPT_FACE",FACE,{"disambiguationData":[OSD([sQuery(id+"F4.wireOp",EDGE,"E13.bottom")])]})]}),makeQuery(id+"F7.opExtrude","SWEPT_FACE",FACE,{"disambiguationData":[OSD([sQuery(id+"F6.wireOp",EDGE,"E19.7.0.3")])]})]});
            var Q9;
            Q9=makeQuery(id+"F7.boolean.opBoolean","INTERSECT",EDGE,{"derivedFrom":[makeQuery(id+"F5.boolean.opBoolean","MERGE",FACE,{"derivedFrom":[makeQuery(id+"F3.boolean.opBoolean","MERGE",FACE,{"derivedFrom":[makeQuery(id+"F1.opExtrude","CAP_FACE",FACE,{"disambiguationData":[OSD([sQuery(id+"F0.wireOp",EDGE,"E0.bottom"),sQuery(id+"F0.wireOp",EDGE,"E0.top"),sQuery(id+"F0.wireOp",EDGE,"E0.left"),sQuery(id+"F0.wireOp",EDGE,"E0.right")])],"isStart":false}),makeQuery(id+"F3.opExtrude","SWEPT_FACE",FACE,{"disambiguationData":[OSD([sQuery(id+"F2.wireOp",EDGE,"E5.bottom")])]}),makeQuery(id+"F3.opExtrude","SWEPT_FACE",FACE,{"disambiguationData":[OSD([sQuery(id+"F2.wireOp",EDGE,"E6.bottom")])]}),makeQuery(id+"F3.opExtrude","SWEPT_FACE",FACE,{"disambiguationData":[OSD([sQuery(id+"F2.wireOp",EDGE,"E7.bottom")])]})]}),makeQuery(id+"F5.opExtrude","SWEPT_FACE",FACE,{"disambiguationData":[OSD([sQuery(id+"F4.wireOp",EDGE,"E11.bottom")])]}),makeQuery(id+"F5.opExtrude","SWEPT_FACE",FACE,{"disambiguationData":[OSD([sQuery(id+"F4.wireOp",EDGE,"E12.bottom")])]}),makeQuery(id+"F5.opExtrude","SWEPT_FACE",FACE,{"disambiguationData":[OSD([sQuery(id+"F4.wireOp",EDGE,"E13.bottom")])]})]}),makeQuery(id+"F7.opExtrude","SWEPT_FACE",FACE,{"disambiguationData":[OSD([sQuery(id+"F6.wireOp",EDGE,"E19.6.0.3")])]})]});
            var Q10;
            Q10=makeQuery(id+"F7.boolean.opBoolean","INTERSECT",EDGE,{"derivedFrom":[makeQuery(id+"F5.boolean.opBoolean","MERGE",FACE,{"derivedFrom":[makeQuery(id+"F3.boolean.opBoolean","MERGE",FACE,{"derivedFrom":[makeQuery(id+"F1.opExtrude","CAP_FACE",FACE,{"disambiguationData":[OSD([sQuery(id+"F0.wireOp",EDGE,"E0.bottom"),sQuery(id+"F0.wireOp",EDGE,"E0.top"),sQuery(id+"F0.wireOp",EDGE,"E0.left"),sQuery(id+"F0.wireOp",EDGE,"E0.right")])],"isStart":false}),makeQuery(id+"F3.opExtrude","SWEPT_FACE",FACE,{"disambiguationData":[OSD([sQuery(id+"F2.wireOp",EDGE,"E5.bottom")])]}),makeQuery(id+"F3.opExtrude","SWEPT_FACE",FACE,{"disambiguationData":[OSD([sQuery(id+"F2.wireOp",EDGE,"E6.bottom")])]}),makeQuery(id+"F3.opExtrude","SWEPT_FACE",FACE,{"disambiguationData":[OSD([sQuery(id+"F2.wireOp",EDGE,"E7.bottom")])]})]}),makeQuery(id+"F5.opExtrude","SWEPT_FACE",FACE,{"disambiguationData":[OSD([sQuery(id+"F4.wireOp",EDGE,"E11.bottom")])]}),makeQuery(id+"F5.opExtrude","SWEPT_FACE",FACE,{"disambiguationData":[OSD([sQuery(id+"F4.wireOp",EDGE,"E12.bottom")])]}),makeQuery(id+"F5.opExtrude","SWEPT_FACE",FACE,{"disambiguationData":[OSD([sQuery(id+"F4.wireOp",EDGE,"E13.bottom")])]})]}),makeQuery(id+"F7.opExtrude","SWEPT_FACE",FACE,{"disambiguationData":[OSD([sQuery(id+"F6.wireOp",EDGE,"E19.5.0.3")])]})]});
            var Q11;
            Q11=makeQuery(id+"F7.boolean.opBoolean","INTERSECT",EDGE,{"derivedFrom":[makeQuery(id+"F5.boolean.opBoolean","MERGE",FACE,{"derivedFrom":[makeQuery(id+"F3.boolean.opBoolean","MERGE",FACE,{"derivedFrom":[makeQuery(id+"F1.opExtrude","CAP_FACE",FACE,{"disambiguationData":[OSD([sQuery(id+"F0.wireOp",EDGE,"E0.bottom"),sQuery(id+"F0.wireOp",EDGE,"E0.top"),sQuery(id+"F0.wireOp",EDGE,"E0.left"),sQuery(id+"F0.wireOp",EDGE,"E0.right")])],"isStart":false}),makeQuery(id+"F3.opExtrude","SWEPT_FACE",FACE,{"disambiguationData":[OSD([sQuery(id+"F2.wireOp",EDGE,"E5.bottom")])]}),makeQuery(id+"F3.opExtrude","SWEPT_FACE",FACE,{"disambiguationData":[OSD([sQuery(id+"F2.wireOp",EDGE,"E6.bottom")])]}),makeQuery(id+"F3.opExtrude","SWEPT_FACE",FACE,{"disambiguationData":[OSD([sQuery(id+"F2.wireOp",EDGE,"E7.bottom")])]})]}),makeQuery(id+"F5.opExtrude","SWEPT_FACE",FACE,{"disambiguationData":[OSD([sQuery(id+"F4.wireOp",EDGE,"E11.bottom")])]}),makeQuery(id+"F5.opExtrude","SWEPT_FACE",FACE,{"disambiguationData":[OSD([sQuery(id+"F4.wireOp",EDGE,"E12.bottom")])]}),makeQuery(id+"F5.opExtrude","SWEPT_FACE",FACE,{"disambiguationData":[OSD([sQuery(id+"F4.wireOp",EDGE,"E13.bottom")])]})]}),makeQuery(id+"F7.opExtrude","SWEPT_FACE",FACE,{"disambiguationData":[OSD([sQuery(id+"F6.wireOp",EDGE,"E19.4.0.3")])]})]});
            var Q12;
            Q12=makeQuery(id+"F7.boolean.opBoolean","INTERSECT",EDGE,{"derivedFrom":[makeQuery(id+"F5.boolean.opBoolean","MERGE",FACE,{"derivedFrom":[makeQuery(id+"F3.boolean.opBoolean","MERGE",FACE,{"derivedFrom":[makeQuery(id+"F1.opExtrude","CAP_FACE",FACE,{"disambiguationData":[OSD([sQuery(id+"F0.wireOp",EDGE,"E0.bottom"),sQuery(id+"F0.wireOp",EDGE,"E0.top"),sQuery(id+"F0.wireOp",EDGE,"E0.left"),sQuery(id+"F0.wireOp",EDGE,"E0.right")])],"isStart":false}),makeQuery(id+"F3.opExtrude","SWEPT_FACE",FACE,{"disambiguationData":[OSD([sQuery(id+"F2.wireOp",EDGE,"E5.bottom")])]}),makeQuery(id+"F3.opExtrude","SWEPT_FACE",FACE,{"disambiguationData":[OSD([sQuery(id+"F2.wireOp",EDGE,"E6.bottom")])]}),makeQuery(id+"F3.opExtrude","SWEPT_FACE",FACE,{"disambiguationData":[OSD([sQuery(id+"F2.wireOp",EDGE,"E7.bottom")])]})]}),makeQuery(id+"F5.opExtrude","SWEPT_FACE",FACE,{"disambiguationData":[OSD([sQuery(id+"F4.wireOp",EDGE,"E11.bottom")])]}),makeQuery(id+"F5.opExtrude","SWEPT_FACE",FACE,{"disambiguationData":[OSD([sQuery(id+"F4.wireOp",EDGE,"E12.bottom")])]}),makeQuery(id+"F5.opExtrude","SWEPT_FACE",FACE,{"disambiguationData":[OSD([sQuery(id+"F4.wireOp",EDGE,"E13.bottom")])]})]}),makeQuery(id+"F7.opExtrude","SWEPT_FACE",FACE,{"disambiguationData":[OSD([sQuery(id+"F6.wireOp",EDGE,"E19.3.0.3")])]})]});
            var Q13;
            Q13=makeQuery(id+"F7.boolean.opBoolean","INTERSECT",EDGE,{"derivedFrom":[makeQuery(id+"F5.boolean.opBoolean","MERGE",FACE,{"derivedFrom":[makeQuery(id+"F3.boolean.opBoolean","MERGE",FACE,{"derivedFrom":[makeQuery(id+"F1.opExtrude","CAP_FACE",FACE,{"disambiguationData":[OSD([sQuery(id+"F0.wireOp",EDGE,"E0.bottom"),sQuery(id+"F0.wireOp",EDGE,"E0.top"),sQuery(id+"F0.wireOp",EDGE,"E0.left"),sQuery(id+"F0.wireOp",EDGE,"E0.right")])],"isStart":false}),makeQuery(id+"F3.opExtrude","SWEPT_FACE",FACE,{"disambiguationData":[OSD([sQuery(id+"F2.wireOp",EDGE,"E5.bottom")])]}),makeQuery(id+"F3.opExtrude","SWEPT_FACE",FACE,{"disambiguationData":[OSD([sQuery(id+"F2.wireOp",EDGE,"E6.bottom")])]}),makeQuery(id+"F3.opExtrude","SWEPT_FACE",FACE,{"disambiguationData":[OSD([sQuery(id+"F2.wireOp",EDGE,"E7.bottom")])]})]}),makeQuery(id+"F5.opExtrude","SWEPT_FACE",FACE,{"disambiguationData":[OSD([sQuery(id+"F4.wireOp",EDGE,"E11.bottom")])]}),makeQuery(id+"F5.opExtrude","SWEPT_FACE",FACE,{"disambiguationData":[OSD([sQuery(id+"F4.wireOp",EDGE,"E12.bottom")])]}),makeQuery(id+"F5.opExtrude","SWEPT_FACE",FACE,{"disambiguationData":[OSD([sQuery(id+"F4.wireOp",EDGE,"E13.bottom")])]})]}),makeQuery(id+"F7.opExtrude","SWEPT_FACE",FACE,{"disambiguationData":[OSD([sQuery(id+"F6.wireOp",EDGE,"E19.2.0.3")])]})]});
            var Q14;
            Q14=makeQuery(id+"F7.boolean.opBoolean","INTERSECT",EDGE,{"derivedFrom":[makeQuery(id+"F5.boolean.opBoolean","MERGE",FACE,{"derivedFrom":[makeQuery(id+"F3.boolean.opBoolean","MERGE",FACE,{"derivedFrom":[makeQuery(id+"F1.opExtrude","CAP_FACE",FACE,{"disambiguationData":[OSD([sQuery(id+"F0.wireOp",EDGE,"E0.bottom"),sQuery(id+"F0.wireOp",EDGE,"E0.top"),sQuery(id+"F0.wireOp",EDGE,"E0.left"),sQuery(id+"F0.wireOp",EDGE,"E0.right")])],"isStart":false}),makeQuery(id+"F3.opExtrude","SWEPT_FACE",FACE,{"disambiguationData":[OSD([sQuery(id+"F2.wireOp",EDGE,"E5.bottom")])]}),makeQuery(id+"F3.opExtrude","SWEPT_FACE",FACE,{"disambiguationData":[OSD([sQuery(id+"F2.wireOp",EDGE,"E6.bottom")])]}),makeQuery(id+"F3.opExtrude","SWEPT_FACE",FACE,{"disambiguationData":[OSD([sQuery(id+"F2.wireOp",EDGE,"E7.bottom")])]})]}),makeQuery(id+"F5.opExtrude","SWEPT_FACE",FACE,{"disambiguationData":[OSD([sQuery(id+"F4.wireOp",EDGE,"E11.bottom")])]}),makeQuery(id+"F5.opExtrude","SWEPT_FACE",FACE,{"disambiguationData":[OSD([sQuery(id+"F4.wireOp",EDGE,"E12.bottom")])]}),makeQuery(id+"F5.opExtrude","SWEPT_FACE",FACE,{"disambiguationData":[OSD([sQuery(id+"F4.wireOp",EDGE,"E13.bottom")])]})]}),makeQuery(id+"F7.opExtrude","SWEPT_FACE",FACE,{"disambiguationData":[OSD([sQuery(id+"F6.wireOp",EDGE,"E19.1.0.3")])]})]});
            var Q15;
            Q15=makeQuery(id+"F7.boolean.opBoolean","INTERSECT",EDGE,{"derivedFrom":[makeQuery(id+"F5.boolean.opBoolean","MERGE",FACE,{"derivedFrom":[makeQuery(id+"F3.boolean.opBoolean","MERGE",FACE,{"derivedFrom":[makeQuery(id+"F1.opExtrude","CAP_FACE",FACE,{"disambiguationData":[OSD([sQuery(id+"F0.wireOp",EDGE,"E0.bottom"),sQuery(id+"F0.wireOp",EDGE,"E0.top"),sQuery(id+"F0.wireOp",EDGE,"E0.left"),sQuery(id+"F0.wireOp",EDGE,"E0.right")])],"isStart":false}),makeQuery(id+"F3.opExtrude","SWEPT_FACE",FACE,{"disambiguationData":[OSD([sQuery(id+"F2.wireOp",EDGE,"E5.bottom")])]}),makeQuery(id+"F3.opExtrude","SWEPT_FACE",FACE,{"disambiguationData":[OSD([sQuery(id+"F2.wireOp",EDGE,"E6.bottom")])]}),makeQuery(id+"F3.opExtrude","SWEPT_FACE",FACE,{"disambiguationData":[OSD([sQuery(id+"F2.wireOp",EDGE,"E7.bottom")])]})]}),makeQuery(id+"F5.opExtrude","SWEPT_FACE",FACE,{"disambiguationData":[OSD([sQuery(id+"F4.wireOp",EDGE,"E11.bottom")])]}),makeQuery(id+"F5.opExtrude","SWEPT_FACE",FACE,{"disambiguationData":[OSD([sQuery(id+"F4.wireOp",EDGE,"E12.bottom")])]}),makeQuery(id+"F5.opExtrude","SWEPT_FACE",FACE,{"disambiguationData":[OSD([sQuery(id+"F4.wireOp",EDGE,"E13.bottom")])]})]}),makeQuery(id+"F7.opExtrude","SWEPT_FACE",FACE,{"disambiguationData":[OSD([sQuery(id+"F6.wireOp",EDGE,"E17")])]})]});
            fillet(context, id + "F8", {"entities" : qUnion([Q0, Q1, Q2, Q3, Q4, Q5, Q6, Q7, Q8, Q9, Q10, Q11, Q12, Q13, Q14, Q15]), "radius" : 5 * mm, "tangentPropagation" : true, "allowEdgeOverflow" : false});
        }
        {
            var Q0;
            Q0=makeQuery(id+"F7.boolean.opBoolean","INTERSECT",EDGE,{"derivedFrom":[makeQuery(id+"F5.boolean.opBoolean","MERGE",FACE,{"derivedFrom":[makeQuery(id+"F3.boolean.opBoolean","MERGE",FACE,{"derivedFrom":[makeQuery(id+"F1.opExtrude","CAP_FACE",FACE,{"disambiguationData":[OSD([sQuery(id+"F0.wireOp",EDGE,"E0.bottom"),sQuery(id+"F0.wireOp",EDGE,"E0.top"),sQuery(id+"F0.wireOp",EDGE,"E0.left"),sQuery(id+"F0.wireOp",EDGE,"E0.right")])],"isStart":false}),makeQuery(id+"F3.opExtrude","SWEPT_FACE",FACE,{"disambiguationData":[OSD([sQuery(id+"F2.wireOp",EDGE,"E5.bottom")])]}),makeQuery(id+"F3.opExtrude","SWEPT_FACE",FACE,{"disambiguationData":[OSD([sQuery(id+"F2.wireOp",EDGE,"E6.bottom")])]}),makeQuery(id+"F3.opExtrude","SWEPT_FACE",FACE,{"disambiguationData":[OSD([sQuery(id+"F2.wireOp",EDGE,"E7.bottom")])]})]}),makeQuery(id+"F5.opExtrude","SWEPT_FACE",FACE,{"disambiguationData":[OSD([sQuery(id+"F4.wireOp",EDGE,"E11.bottom")])]}),makeQuery(id+"F5.opExtrude","SWEPT_FACE",FACE,{"disambiguationData":[OSD([sQuery(id+"F4.wireOp",EDGE,"E12.bottom")])]}),makeQuery(id+"F5.opExtrude","SWEPT_FACE",FACE,{"disambiguationData":[OSD([sQuery(id+"F4.wireOp",EDGE,"E13.bottom")])]})]}),makeQuery(id+"F7.opExtrude","SWEPT_FACE",FACE,{"disambiguationData":[OSD([sQuery(id+"F6.wireOp",EDGE,"E16")])]})]});
            var Q1;
            Q1=makeQuery(id+"F7.boolean.opBoolean","INTERSECT",EDGE,{"derivedFrom":[makeQuery(id+"F5.boolean.opBoolean","MERGE",FACE,{"derivedFrom":[makeQuery(id+"F3.boolean.opBoolean","MERGE",FACE,{"derivedFrom":[makeQuery(id+"F1.opExtrude","CAP_FACE",FACE,{"disambiguationData":[OSD([sQuery(id+"F0.wireOp",EDGE,"E0.bottom"),sQuery(id+"F0.wireOp",EDGE,"E0.top"),sQuery(id+"F0.wireOp",EDGE,"E0.left"),sQuery(id+"F0.wireOp",EDGE,"E0.right")])],"isStart":false}),makeQuery(id+"F3.opExtrude","SWEPT_FACE",FACE,{"disambiguationData":[OSD([sQuery(id+"F2.wireOp",EDGE,"E5.bottom")])]}),makeQuery(id+"F3.opExtrude","SWEPT_FACE",FACE,{"disambiguationData":[OSD([sQuery(id+"F2.wireOp",EDGE,"E6.bottom")])]}),makeQuery(id+"F3.opExtrude","SWEPT_FACE",FACE,{"disambiguationData":[OSD([sQuery(id+"F2.wireOp",EDGE,"E7.bottom")])]})]}),makeQuery(id+"F5.opExtrude","SWEPT_FACE",FACE,{"disambiguationData":[OSD([sQuery(id+"F4.wireOp",EDGE,"E11.bottom")])]}),makeQuery(id+"F5.opExtrude","SWEPT_FACE",FACE,{"disambiguationData":[OSD([sQuery(id+"F4.wireOp",EDGE,"E12.bottom")])]}),makeQuery(id+"F5.opExtrude","SWEPT_FACE",FACE,{"disambiguationData":[OSD([sQuery(id+"F4.wireOp",EDGE,"E13.bottom")])]})]}),makeQuery(id+"F7.opExtrude","SWEPT_FACE",FACE,{"disambiguationData":[OSD([sQuery(id+"F6.wireOp",EDGE,"E19.1.0.2")])]})]});
            var Q2;
            Q2=makeQuery(id+"F7.boolean.opBoolean","INTERSECT",EDGE,{"derivedFrom":[makeQuery(id+"F5.boolean.opBoolean","MERGE",FACE,{"derivedFrom":[makeQuery(id+"F3.boolean.opBoolean","MERGE",FACE,{"derivedFrom":[makeQuery(id+"F1.opExtrude","CAP_FACE",FACE,{"disambiguationData":[OSD([sQuery(id+"F0.wireOp",EDGE,"E0.bottom"),sQuery(id+"F0.wireOp",EDGE,"E0.top"),sQuery(id+"F0.wireOp",EDGE,"E0.left"),sQuery(id+"F0.wireOp",EDGE,"E0.right")])],"isStart":false}),makeQuery(id+"F3.opExtrude","SWEPT_FACE",FACE,{"disambiguationData":[OSD([sQuery(id+"F2.wireOp",EDGE,"E5.bottom")])]}),makeQuery(id+"F3.opExtrude","SWEPT_FACE",FACE,{"disambiguationData":[OSD([sQuery(id+"F2.wireOp",EDGE,"E6.bottom")])]}),makeQuery(id+"F3.opExtrude","SWEPT_FACE",FACE,{"disambiguationData":[OSD([sQuery(id+"F2.wireOp",EDGE,"E7.bottom")])]})]}),makeQuery(id+"F5.opExtrude","SWEPT_FACE",FACE,{"disambiguationData":[OSD([sQuery(id+"F4.wireOp",EDGE,"E11.bottom")])]}),makeQuery(id+"F5.opExtrude","SWEPT_FACE",FACE,{"disambiguationData":[OSD([sQuery(id+"F4.wireOp",EDGE,"E12.bottom")])]}),makeQuery(id+"F5.opExtrude","SWEPT_FACE",FACE,{"disambiguationData":[OSD([sQuery(id+"F4.wireOp",EDGE,"E13.bottom")])]})]}),makeQuery(id+"F7.opExtrude","SWEPT_FACE",FACE,{"disambiguationData":[OSD([sQuery(id+"F6.wireOp",EDGE,"E19.2.0.2")])]})]});
            var Q3;
            Q3=makeQuery(id+"F7.boolean.opBoolean","INTERSECT",EDGE,{"derivedFrom":[makeQuery(id+"F5.boolean.opBoolean","MERGE",FACE,{"derivedFrom":[makeQuery(id+"F3.boolean.opBoolean","MERGE",FACE,{"derivedFrom":[makeQuery(id+"F1.opExtrude","CAP_FACE",FACE,{"disambiguationData":[OSD([sQuery(id+"F0.wireOp",EDGE,"E0.bottom"),sQuery(id+"F0.wireOp",EDGE,"E0.top"),sQuery(id+"F0.wireOp",EDGE,"E0.left"),sQuery(id+"F0.wireOp",EDGE,"E0.right")])],"isStart":false}),makeQuery(id+"F3.opExtrude","SWEPT_FACE",FACE,{"disambiguationData":[OSD([sQuery(id+"F2.wireOp",EDGE,"E5.bottom")])]}),makeQuery(id+"F3.opExtrude","SWEPT_FACE",FACE,{"disambiguationData":[OSD([sQuery(id+"F2.wireOp",EDGE,"E6.bottom")])]}),makeQuery(id+"F3.opExtrude","SWEPT_FACE",FACE,{"disambiguationData":[OSD([sQuery(id+"F2.wireOp",EDGE,"E7.bottom")])]})]}),makeQuery(id+"F5.opExtrude","SWEPT_FACE",FACE,{"disambiguationData":[OSD([sQuery(id+"F4.wireOp",EDGE,"E11.bottom")])]}),makeQuery(id+"F5.opExtrude","SWEPT_FACE",FACE,{"disambiguationData":[OSD([sQuery(id+"F4.wireOp",EDGE,"E12.bottom")])]}),makeQuery(id+"F5.opExtrude","SWEPT_FACE",FACE,{"disambiguationData":[OSD([sQuery(id+"F4.wireOp",EDGE,"E13.bottom")])]})]}),makeQuery(id+"F7.opExtrude","SWEPT_FACE",FACE,{"disambiguationData":[OSD([sQuery(id+"F6.wireOp",EDGE,"E19.3.0.2")])]})]});
            var Q4;
            Q4=makeQuery(id+"F7.boolean.opBoolean","INTERSECT",EDGE,{"derivedFrom":[makeQuery(id+"F5.boolean.opBoolean","MERGE",FACE,{"derivedFrom":[makeQuery(id+"F3.boolean.opBoolean","MERGE",FACE,{"derivedFrom":[makeQuery(id+"F1.opExtrude","CAP_FACE",FACE,{"disambiguationData":[OSD([sQuery(id+"F0.wireOp",EDGE,"E0.bottom"),sQuery(id+"F0.wireOp",EDGE,"E0.top"),sQuery(id+"F0.wireOp",EDGE,"E0.left"),sQuery(id+"F0.wireOp",EDGE,"E0.right")])],"isStart":false}),makeQuery(id+"F3.opExtrude","SWEPT_FACE",FACE,{"disambiguationData":[OSD([sQuery(id+"F2.wireOp",EDGE,"E5.bottom")])]}),makeQuery(id+"F3.opExtrude","SWEPT_FACE",FACE,{"disambiguationData":[OSD([sQuery(id+"F2.wireOp",EDGE,"E6.bottom")])]}),makeQuery(id+"F3.opExtrude","SWEPT_FACE",FACE,{"disambiguationData":[OSD([sQuery(id+"F2.wireOp",EDGE,"E7.bottom")])]})]}),makeQuery(id+"F5.opExtrude","SWEPT_FACE",FACE,{"disambiguationData":[OSD([sQuery(id+"F4.wireOp",EDGE,"E11.bottom")])]}),makeQuery(id+"F5.opExtrude","SWEPT_FACE",FACE,{"disambiguationData":[OSD([sQuery(id+"F4.wireOp",EDGE,"E12.bottom")])]}),makeQuery(id+"F5.opExtrude","SWEPT_FACE",FACE,{"disambiguationData":[OSD([sQuery(id+"F4.wireOp",EDGE,"E13.bottom")])]})]}),makeQuery(id+"F7.opExtrude","SWEPT_FACE",FACE,{"disambiguationData":[OSD([sQuery(id+"F6.wireOp",EDGE,"E19.4.0.2")])]})]});
            var Q5;
            Q5=makeQuery(id+"F7.boolean.opBoolean","INTERSECT",EDGE,{"derivedFrom":[makeQuery(id+"F5.boolean.opBoolean","MERGE",FACE,{"derivedFrom":[makeQuery(id+"F3.boolean.opBoolean","MERGE",FACE,{"derivedFrom":[makeQuery(id+"F1.opExtrude","CAP_FACE",FACE,{"disambiguationData":[OSD([sQuery(id+"F0.wireOp",EDGE,"E0.bottom"),sQuery(id+"F0.wireOp",EDGE,"E0.top"),sQuery(id+"F0.wireOp",EDGE,"E0.left"),sQuery(id+"F0.wireOp",EDGE,"E0.right")])],"isStart":false}),makeQuery(id+"F3.opExtrude","SWEPT_FACE",FACE,{"disambiguationData":[OSD([sQuery(id+"F2.wireOp",EDGE,"E5.bottom")])]}),makeQuery(id+"F3.opExtrude","SWEPT_FACE",FACE,{"disambiguationData":[OSD([sQuery(id+"F2.wireOp",EDGE,"E6.bottom")])]}),makeQuery(id+"F3.opExtrude","SWEPT_FACE",FACE,{"disambiguationData":[OSD([sQuery(id+"F2.wireOp",EDGE,"E7.bottom")])]})]}),makeQuery(id+"F5.opExtrude","SWEPT_FACE",FACE,{"disambiguationData":[OSD([sQuery(id+"F4.wireOp",EDGE,"E11.bottom")])]}),makeQuery(id+"F5.opExtrude","SWEPT_FACE",FACE,{"disambiguationData":[OSD([sQuery(id+"F4.wireOp",EDGE,"E12.bottom")])]}),makeQuery(id+"F5.opExtrude","SWEPT_FACE",FACE,{"disambiguationData":[OSD([sQuery(id+"F4.wireOp",EDGE,"E13.bottom")])]})]}),makeQuery(id+"F7.opExtrude","SWEPT_FACE",FACE,{"disambiguationData":[OSD([sQuery(id+"F6.wireOp",EDGE,"E19.5.0.2")])]})]});
            var Q6;
            Q6=makeQuery(id+"F7.boolean.opBoolean","INTERSECT",EDGE,{"derivedFrom":[makeQuery(id+"F5.boolean.opBoolean","MERGE",FACE,{"derivedFrom":[makeQuery(id+"F3.boolean.opBoolean","MERGE",FACE,{"derivedFrom":[makeQuery(id+"F1.opExtrude","CAP_FACE",FACE,{"disambiguationData":[OSD([sQuery(id+"F0.wireOp",EDGE,"E0.bottom"),sQuery(id+"F0.wireOp",EDGE,"E0.top"),sQuery(id+"F0.wireOp",EDGE,"E0.left"),sQuery(id+"F0.wireOp",EDGE,"E0.right")])],"isStart":false}),makeQuery(id+"F3.opExtrude","SWEPT_FACE",FACE,{"disambiguationData":[OSD([sQuery(id+"F2.wireOp",EDGE,"E5.bottom")])]}),makeQuery(id+"F3.opExtrude","SWEPT_FACE",FACE,{"disambiguationData":[OSD([sQuery(id+"F2.wireOp",EDGE,"E6.bottom")])]}),makeQuery(id+"F3.opExtrude","SWEPT_FACE",FACE,{"disambiguationData":[OSD([sQuery(id+"F2.wireOp",EDGE,"E7.bottom")])]})]}),makeQuery(id+"F5.opExtrude","SWEPT_FACE",FACE,{"disambiguationData":[OSD([sQuery(id+"F4.wireOp",EDGE,"E11.bottom")])]}),makeQuery(id+"F5.opExtrude","SWEPT_FACE",FACE,{"disambiguationData":[OSD([sQuery(id+"F4.wireOp",EDGE,"E12.bottom")])]}),makeQuery(id+"F5.opExtrude","SWEPT_FACE",FACE,{"disambiguationData":[OSD([sQuery(id+"F4.wireOp",EDGE,"E13.bottom")])]})]}),makeQuery(id+"F7.opExtrude","SWEPT_FACE",FACE,{"disambiguationData":[OSD([sQuery(id+"F6.wireOp",EDGE,"E19.6.0.2")])]})]});
            var Q7;
            Q7=makeQuery(id+"F7.boolean.opBoolean","INTERSECT",EDGE,{"derivedFrom":[makeQuery(id+"F5.boolean.opBoolean","MERGE",FACE,{"derivedFrom":[makeQuery(id+"F3.boolean.opBoolean","MERGE",FACE,{"derivedFrom":[makeQuery(id+"F1.opExtrude","CAP_FACE",FACE,{"disambiguationData":[OSD([sQuery(id+"F0.wireOp",EDGE,"E0.bottom"),sQuery(id+"F0.wireOp",EDGE,"E0.top"),sQuery(id+"F0.wireOp",EDGE,"E0.left"),sQuery(id+"F0.wireOp",EDGE,"E0.right")])],"isStart":false}),makeQuery(id+"F3.opExtrude","SWEPT_FACE",FACE,{"disambiguationData":[OSD([sQuery(id+"F2.wireOp",EDGE,"E5.bottom")])]}),makeQuery(id+"F3.opExtrude","SWEPT_FACE",FACE,{"disambiguationData":[OSD([sQuery(id+"F2.wireOp",EDGE,"E6.bottom")])]}),makeQuery(id+"F3.opExtrude","SWEPT_FACE",FACE,{"disambiguationData":[OSD([sQuery(id+"F2.wireOp",EDGE,"E7.bottom")])]})]}),makeQuery(id+"F5.opExtrude","SWEPT_FACE",FACE,{"disambiguationData":[OSD([sQuery(id+"F4.wireOp",EDGE,"E11.bottom")])]}),makeQuery(id+"F5.opExtrude","SWEPT_FACE",FACE,{"disambiguationData":[OSD([sQuery(id+"F4.wireOp",EDGE,"E12.bottom")])]}),makeQuery(id+"F5.opExtrude","SWEPT_FACE",FACE,{"disambiguationData":[OSD([sQuery(id+"F4.wireOp",EDGE,"E13.bottom")])]})]}),makeQuery(id+"F7.opExtrude","SWEPT_FACE",FACE,{"disambiguationData":[OSD([sQuery(id+"F6.wireOp",EDGE,"E19.7.0.2")])]})]});
            var Q8;
            Q8=makeQuery(id+"F7.boolean.opBoolean","INTERSECT",EDGE,{"derivedFrom":[makeQuery(id+"F5.boolean.opBoolean","MERGE",FACE,{"derivedFrom":[makeQuery(id+"F3.boolean.opBoolean","MERGE",FACE,{"derivedFrom":[makeQuery(id+"F1.opExtrude","CAP_FACE",FACE,{"disambiguationData":[OSD([sQuery(id+"F0.wireOp",EDGE,"E0.bottom"),sQuery(id+"F0.wireOp",EDGE,"E0.top"),sQuery(id+"F0.wireOp",EDGE,"E0.left"),sQuery(id+"F0.wireOp",EDGE,"E0.right")])],"isStart":false}),makeQuery(id+"F3.opExtrude","SWEPT_FACE",FACE,{"disambiguationData":[OSD([sQuery(id+"F2.wireOp",EDGE,"E5.bottom")])]}),makeQuery(id+"F3.opExtrude","SWEPT_FACE",FACE,{"disambiguationData":[OSD([sQuery(id+"F2.wireOp",EDGE,"E6.bottom")])]}),makeQuery(id+"F3.opExtrude","SWEPT_FACE",FACE,{"disambiguationData":[OSD([sQuery(id+"F2.wireOp",EDGE,"E7.bottom")])]})]}),makeQuery(id+"F5.opExtrude","SWEPT_FACE",FACE,{"disambiguationData":[OSD([sQuery(id+"F4.wireOp",EDGE,"E11.bottom")])]}),makeQuery(id+"F5.opExtrude","SWEPT_FACE",FACE,{"disambiguationData":[OSD([sQuery(id+"F4.wireOp",EDGE,"E12.bottom")])]}),makeQuery(id+"F5.opExtrude","SWEPT_FACE",FACE,{"disambiguationData":[OSD([sQuery(id+"F4.wireOp",EDGE,"E13.bottom")])]})]}),makeQuery(id+"F7.opExtrude","SWEPT_FACE",FACE,{"disambiguationData":[OSD([sQuery(id+"F6.wireOp",EDGE,"E19.7.0.1")])]})]});
            var Q9;
            Q9=makeQuery(id+"F7.boolean.opBoolean","INTERSECT",EDGE,{"derivedFrom":[makeQuery(id+"F5.boolean.opBoolean","MERGE",FACE,{"derivedFrom":[makeQuery(id+"F3.boolean.opBoolean","MERGE",FACE,{"derivedFrom":[makeQuery(id+"F1.opExtrude","CAP_FACE",FACE,{"disambiguationData":[OSD([sQuery(id+"F0.wireOp",EDGE,"E0.bottom"),sQuery(id+"F0.wireOp",EDGE,"E0.top"),sQuery(id+"F0.wireOp",EDGE,"E0.left"),sQuery(id+"F0.wireOp",EDGE,"E0.right")])],"isStart":false}),makeQuery(id+"F3.opExtrude","SWEPT_FACE",FACE,{"disambiguationData":[OSD([sQuery(id+"F2.wireOp",EDGE,"E5.bottom")])]}),makeQuery(id+"F3.opExtrude","SWEPT_FACE",FACE,{"disambiguationData":[OSD([sQuery(id+"F2.wireOp",EDGE,"E6.bottom")])]}),makeQuery(id+"F3.opExtrude","SWEPT_FACE",FACE,{"disambiguationData":[OSD([sQuery(id+"F2.wireOp",EDGE,"E7.bottom")])]})]}),makeQuery(id+"F5.opExtrude","SWEPT_FACE",FACE,{"disambiguationData":[OSD([sQuery(id+"F4.wireOp",EDGE,"E11.bottom")])]}),makeQuery(id+"F5.opExtrude","SWEPT_FACE",FACE,{"disambiguationData":[OSD([sQuery(id+"F4.wireOp",EDGE,"E12.bottom")])]}),makeQuery(id+"F5.opExtrude","SWEPT_FACE",FACE,{"disambiguationData":[OSD([sQuery(id+"F4.wireOp",EDGE,"E13.bottom")])]})]}),makeQuery(id+"F7.opExtrude","SWEPT_FACE",FACE,{"disambiguationData":[OSD([sQuery(id+"F6.wireOp",EDGE,"E19.6.0.1")])]})]});
            var Q10;
            Q10=makeQuery(id+"F7.boolean.opBoolean","INTERSECT",EDGE,{"derivedFrom":[makeQuery(id+"F5.boolean.opBoolean","MERGE",FACE,{"derivedFrom":[makeQuery(id+"F3.boolean.opBoolean","MERGE",FACE,{"derivedFrom":[makeQuery(id+"F1.opExtrude","CAP_FACE",FACE,{"disambiguationData":[OSD([sQuery(id+"F0.wireOp",EDGE,"E0.bottom"),sQuery(id+"F0.wireOp",EDGE,"E0.top"),sQuery(id+"F0.wireOp",EDGE,"E0.left"),sQuery(id+"F0.wireOp",EDGE,"E0.right")])],"isStart":false}),makeQuery(id+"F3.opExtrude","SWEPT_FACE",FACE,{"disambiguationData":[OSD([sQuery(id+"F2.wireOp",EDGE,"E5.bottom")])]}),makeQuery(id+"F3.opExtrude","SWEPT_FACE",FACE,{"disambiguationData":[OSD([sQuery(id+"F2.wireOp",EDGE,"E6.bottom")])]}),makeQuery(id+"F3.opExtrude","SWEPT_FACE",FACE,{"disambiguationData":[OSD([sQuery(id+"F2.wireOp",EDGE,"E7.bottom")])]})]}),makeQuery(id+"F5.opExtrude","SWEPT_FACE",FACE,{"disambiguationData":[OSD([sQuery(id+"F4.wireOp",EDGE,"E11.bottom")])]}),makeQuery(id+"F5.opExtrude","SWEPT_FACE",FACE,{"disambiguationData":[OSD([sQuery(id+"F4.wireOp",EDGE,"E12.bottom")])]}),makeQuery(id+"F5.opExtrude","SWEPT_FACE",FACE,{"disambiguationData":[OSD([sQuery(id+"F4.wireOp",EDGE,"E13.bottom")])]})]}),makeQuery(id+"F7.opExtrude","SWEPT_FACE",FACE,{"disambiguationData":[OSD([sQuery(id+"F6.wireOp",EDGE,"E19.5.0.1")])]})]});
            var Q11;
            Q11=makeQuery(id+"F7.boolean.opBoolean","INTERSECT",EDGE,{"derivedFrom":[makeQuery(id+"F5.boolean.opBoolean","MERGE",FACE,{"derivedFrom":[makeQuery(id+"F3.boolean.opBoolean","MERGE",FACE,{"derivedFrom":[makeQuery(id+"F1.opExtrude","CAP_FACE",FACE,{"disambiguationData":[OSD([sQuery(id+"F0.wireOp",EDGE,"E0.bottom"),sQuery(id+"F0.wireOp",EDGE,"E0.top"),sQuery(id+"F0.wireOp",EDGE,"E0.left"),sQuery(id+"F0.wireOp",EDGE,"E0.right")])],"isStart":false}),makeQuery(id+"F3.opExtrude","SWEPT_FACE",FACE,{"disambiguationData":[OSD([sQuery(id+"F2.wireOp",EDGE,"E5.bottom")])]}),makeQuery(id+"F3.opExtrude","SWEPT_FACE",FACE,{"disambiguationData":[OSD([sQuery(id+"F2.wireOp",EDGE,"E6.bottom")])]}),makeQuery(id+"F3.opExtrude","SWEPT_FACE",FACE,{"disambiguationData":[OSD([sQuery(id+"F2.wireOp",EDGE,"E7.bottom")])]})]}),makeQuery(id+"F5.opExtrude","SWEPT_FACE",FACE,{"disambiguationData":[OSD([sQuery(id+"F4.wireOp",EDGE,"E11.bottom")])]}),makeQuery(id+"F5.opExtrude","SWEPT_FACE",FACE,{"disambiguationData":[OSD([sQuery(id+"F4.wireOp",EDGE,"E12.bottom")])]}),makeQuery(id+"F5.opExtrude","SWEPT_FACE",FACE,{"disambiguationData":[OSD([sQuery(id+"F4.wireOp",EDGE,"E13.bottom")])]})]}),makeQuery(id+"F7.opExtrude","SWEPT_FACE",FACE,{"disambiguationData":[OSD([sQuery(id+"F6.wireOp",EDGE,"E19.4.0.1")])]})]});
            var Q12;
            Q12=makeQuery(id+"F7.boolean.opBoolean","INTERSECT",EDGE,{"derivedFrom":[makeQuery(id+"F5.boolean.opBoolean","MERGE",FACE,{"derivedFrom":[makeQuery(id+"F3.boolean.opBoolean","MERGE",FACE,{"derivedFrom":[makeQuery(id+"F1.opExtrude","CAP_FACE",FACE,{"disambiguationData":[OSD([sQuery(id+"F0.wireOp",EDGE,"E0.bottom"),sQuery(id+"F0.wireOp",EDGE,"E0.top"),sQuery(id+"F0.wireOp",EDGE,"E0.left"),sQuery(id+"F0.wireOp",EDGE,"E0.right")])],"isStart":false}),makeQuery(id+"F3.opExtrude","SWEPT_FACE",FACE,{"disambiguationData":[OSD([sQuery(id+"F2.wireOp",EDGE,"E5.bottom")])]}),makeQuery(id+"F3.opExtrude","SWEPT_FACE",FACE,{"disambiguationData":[OSD([sQuery(id+"F2.wireOp",EDGE,"E6.bottom")])]}),makeQuery(id+"F3.opExtrude","SWEPT_FACE",FACE,{"disambiguationData":[OSD([sQuery(id+"F2.wireOp",EDGE,"E7.bottom")])]})]}),makeQuery(id+"F5.opExtrude","SWEPT_FACE",FACE,{"disambiguationData":[OSD([sQuery(id+"F4.wireOp",EDGE,"E11.bottom")])]}),makeQuery(id+"F5.opExtrude","SWEPT_FACE",FACE,{"disambiguationData":[OSD([sQuery(id+"F4.wireOp",EDGE,"E12.bottom")])]}),makeQuery(id+"F5.opExtrude","SWEPT_FACE",FACE,{"disambiguationData":[OSD([sQuery(id+"F4.wireOp",EDGE,"E13.bottom")])]})]}),makeQuery(id+"F7.opExtrude","SWEPT_FACE",FACE,{"disambiguationData":[OSD([sQuery(id+"F6.wireOp",EDGE,"E19.3.0.1")])]})]});
            var Q13;
            Q13=makeQuery(id+"F7.boolean.opBoolean","INTERSECT",EDGE,{"derivedFrom":[makeQuery(id+"F5.boolean.opBoolean","MERGE",FACE,{"derivedFrom":[makeQuery(id+"F3.boolean.opBoolean","MERGE",FACE,{"derivedFrom":[makeQuery(id+"F1.opExtrude","CAP_FACE",FACE,{"disambiguationData":[OSD([sQuery(id+"F0.wireOp",EDGE,"E0.bottom"),sQuery(id+"F0.wireOp",EDGE,"E0.top"),sQuery(id+"F0.wireOp",EDGE,"E0.left"),sQuery(id+"F0.wireOp",EDGE,"E0.right")])],"isStart":false}),makeQuery(id+"F3.opExtrude","SWEPT_FACE",FACE,{"disambiguationData":[OSD([sQuery(id+"F2.wireOp",EDGE,"E5.bottom")])]}),makeQuery(id+"F3.opExtrude","SWEPT_FACE",FACE,{"disambiguationData":[OSD([sQuery(id+"F2.wireOp",EDGE,"E6.bottom")])]}),makeQuery(id+"F3.opExtrude","SWEPT_FACE",FACE,{"disambiguationData":[OSD([sQuery(id+"F2.wireOp",EDGE,"E7.bottom")])]})]}),makeQuery(id+"F5.opExtrude","SWEPT_FACE",FACE,{"disambiguationData":[OSD([sQuery(id+"F4.wireOp",EDGE,"E11.bottom")])]}),makeQuery(id+"F5.opExtrude","SWEPT_FACE",FACE,{"disambiguationData":[OSD([sQuery(id+"F4.wireOp",EDGE,"E12.bottom")])]}),makeQuery(id+"F5.opExtrude","SWEPT_FACE",FACE,{"disambiguationData":[OSD([sQuery(id+"F4.wireOp",EDGE,"E13.bottom")])]})]}),makeQuery(id+"F7.opExtrude","SWEPT_FACE",FACE,{"disambiguationData":[OSD([sQuery(id+"F6.wireOp",EDGE,"E19.2.0.1")])]})]});
            var Q14;
            Q14=makeQuery(id+"F7.boolean.opBoolean","INTERSECT",EDGE,{"derivedFrom":[makeQuery(id+"F5.boolean.opBoolean","MERGE",FACE,{"derivedFrom":[makeQuery(id+"F3.boolean.opBoolean","MERGE",FACE,{"derivedFrom":[makeQuery(id+"F1.opExtrude","CAP_FACE",FACE,{"disambiguationData":[OSD([sQuery(id+"F0.wireOp",EDGE,"E0.bottom"),sQuery(id+"F0.wireOp",EDGE,"E0.top"),sQuery(id+"F0.wireOp",EDGE,"E0.left"),sQuery(id+"F0.wireOp",EDGE,"E0.right")])],"isStart":false}),makeQuery(id+"F3.opExtrude","SWEPT_FACE",FACE,{"disambiguationData":[OSD([sQuery(id+"F2.wireOp",EDGE,"E5.bottom")])]}),makeQuery(id+"F3.opExtrude","SWEPT_FACE",FACE,{"disambiguationData":[OSD([sQuery(id+"F2.wireOp",EDGE,"E6.bottom")])]}),makeQuery(id+"F3.opExtrude","SWEPT_FACE",FACE,{"disambiguationData":[OSD([sQuery(id+"F2.wireOp",EDGE,"E7.bottom")])]})]}),makeQuery(id+"F5.opExtrude","SWEPT_FACE",FACE,{"disambiguationData":[OSD([sQuery(id+"F4.wireOp",EDGE,"E11.bottom")])]}),makeQuery(id+"F5.opExtrude","SWEPT_FACE",FACE,{"disambiguationData":[OSD([sQuery(id+"F4.wireOp",EDGE,"E12.bottom")])]}),makeQuery(id+"F5.opExtrude","SWEPT_FACE",FACE,{"disambiguationData":[OSD([sQuery(id+"F4.wireOp",EDGE,"E13.bottom")])]})]}),makeQuery(id+"F7.opExtrude","SWEPT_FACE",FACE,{"disambiguationData":[OSD([sQuery(id+"F6.wireOp",EDGE,"E19.1.0.1")])]})]});
            var Q15;
            Q15=makeQuery(id+"F7.boolean.opBoolean","INTERSECT",EDGE,{"derivedFrom":[makeQuery(id+"F5.boolean.opBoolean","MERGE",FACE,{"derivedFrom":[makeQuery(id+"F3.boolean.opBoolean","MERGE",FACE,{"derivedFrom":[makeQuery(id+"F1.opExtrude","CAP_FACE",FACE,{"disambiguationData":[OSD([sQuery(id+"F0.wireOp",EDGE,"E0.bottom"),sQuery(id+"F0.wireOp",EDGE,"E0.top"),sQuery(id+"F0.wireOp",EDGE,"E0.left"),sQuery(id+"F0.wireOp",EDGE,"E0.right")])],"isStart":false}),makeQuery(id+"F3.opExtrude","SWEPT_FACE",FACE,{"disambiguationData":[OSD([sQuery(id+"F2.wireOp",EDGE,"E5.bottom")])]}),makeQuery(id+"F3.opExtrude","SWEPT_FACE",FACE,{"disambiguationData":[OSD([sQuery(id+"F2.wireOp",EDGE,"E6.bottom")])]}),makeQuery(id+"F3.opExtrude","SWEPT_FACE",FACE,{"disambiguationData":[OSD([sQuery(id+"F2.wireOp",EDGE,"E7.bottom")])]})]}),makeQuery(id+"F5.opExtrude","SWEPT_FACE",FACE,{"disambiguationData":[OSD([sQuery(id+"F4.wireOp",EDGE,"E11.bottom")])]}),makeQuery(id+"F5.opExtrude","SWEPT_FACE",FACE,{"disambiguationData":[OSD([sQuery(id+"F4.wireOp",EDGE,"E12.bottom")])]}),makeQuery(id+"F5.opExtrude","SWEPT_FACE",FACE,{"disambiguationData":[OSD([sQuery(id+"F4.wireOp",EDGE,"E13.bottom")])]})]}),makeQuery(id+"F7.opExtrude","SWEPT_FACE",FACE,{"disambiguationData":[OSD([sQuery(id+"F6.wireOp",EDGE,"E15")])]})]});
            var Q16;
            Q16=makeQuery(id+"F7.boolean.opBoolean","INTERSECT",EDGE,{"derivedFrom":[makeQuery(id+"F5.boolean.opBoolean","MERGE",FACE,{"derivedFrom":[makeQuery(id+"F3.boolean.opBoolean","MERGE",FACE,{"derivedFrom":[makeQuery(id+"F1.opExtrude","CAP_FACE",FACE,{"disambiguationData":[OSD([sQuery(id+"F0.wireOp",EDGE,"E0.bottom"),sQuery(id+"F0.wireOp",EDGE,"E0.top"),sQuery(id+"F0.wireOp",EDGE,"E0.left"),sQuery(id+"F0.wireOp",EDGE,"E0.right")])],"isStart":false}),makeQuery(id+"F3.opExtrude","SWEPT_FACE",FACE,{"disambiguationData":[OSD([sQuery(id+"F2.wireOp",EDGE,"E5.bottom")])]}),makeQuery(id+"F3.opExtrude","SWEPT_FACE",FACE,{"disambiguationData":[OSD([sQuery(id+"F2.wireOp",EDGE,"E6.bottom")])]}),makeQuery(id+"F3.opExtrude","SWEPT_FACE",FACE,{"disambiguationData":[OSD([sQuery(id+"F2.wireOp",EDGE,"E7.bottom")])]})]}),makeQuery(id+"F5.opExtrude","SWEPT_FACE",FACE,{"disambiguationData":[OSD([sQuery(id+"F4.wireOp",EDGE,"E11.bottom")])]}),makeQuery(id+"F5.opExtrude","SWEPT_FACE",FACE,{"disambiguationData":[OSD([sQuery(id+"F4.wireOp",EDGE,"E12.bottom")])]}),makeQuery(id+"F5.opExtrude","SWEPT_FACE",FACE,{"disambiguationData":[OSD([sQuery(id+"F4.wireOp",EDGE,"E13.bottom")])]})]}),makeQuery(id+"F7.opExtrude","SWEPT_FACE",FACE,{"disambiguationData":[OSD([sQuery(id+"F6.wireOp",EDGE,"E14")])]})]});
            var Q17;
            Q17=makeQuery(id+"F7.boolean.opBoolean","INTERSECT",EDGE,{"derivedFrom":[makeQuery(id+"F5.boolean.opBoolean","MERGE",FACE,{"derivedFrom":[makeQuery(id+"F3.boolean.opBoolean","MERGE",FACE,{"derivedFrom":[makeQuery(id+"F1.opExtrude","CAP_FACE",FACE,{"disambiguationData":[OSD([sQuery(id+"F0.wireOp",EDGE,"E0.bottom"),sQuery(id+"F0.wireOp",EDGE,"E0.top"),sQuery(id+"F0.wireOp",EDGE,"E0.left"),sQuery(id+"F0.wireOp",EDGE,"E0.right")])],"isStart":false}),makeQuery(id+"F3.opExtrude","SWEPT_FACE",FACE,{"disambiguationData":[OSD([sQuery(id+"F2.wireOp",EDGE,"E5.bottom")])]}),makeQuery(id+"F3.opExtrude","SWEPT_FACE",FACE,{"disambiguationData":[OSD([sQuery(id+"F2.wireOp",EDGE,"E6.bottom")])]}),makeQuery(id+"F3.opExtrude","SWEPT_FACE",FACE,{"disambiguationData":[OSD([sQuery(id+"F2.wireOp",EDGE,"E7.bottom")])]})]}),makeQuery(id+"F5.opExtrude","SWEPT_FACE",FACE,{"disambiguationData":[OSD([sQuery(id+"F4.wireOp",EDGE,"E11.bottom")])]}),makeQuery(id+"F5.opExtrude","SWEPT_FACE",FACE,{"disambiguationData":[OSD([sQuery(id+"F4.wireOp",EDGE,"E12.bottom")])]}),makeQuery(id+"F5.opExtrude","SWEPT_FACE",FACE,{"disambiguationData":[OSD([sQuery(id+"F4.wireOp",EDGE,"E13.bottom")])]})]}),makeQuery(id+"F7.opExtrude","SWEPT_FACE",FACE,{"disambiguationData":[OSD([sQuery(id+"F6.wireOp",EDGE,"E19.1.0.0")])]})]});
            var Q18;
            Q18=makeQuery(id+"F7.boolean.opBoolean","INTERSECT",EDGE,{"derivedFrom":[makeQuery(id+"F5.boolean.opBoolean","MERGE",FACE,{"derivedFrom":[makeQuery(id+"F3.boolean.opBoolean","MERGE",FACE,{"derivedFrom":[makeQuery(id+"F1.opExtrude","CAP_FACE",FACE,{"disambiguationData":[OSD([sQuery(id+"F0.wireOp",EDGE,"E0.bottom"),sQuery(id+"F0.wireOp",EDGE,"E0.top"),sQuery(id+"F0.wireOp",EDGE,"E0.left"),sQuery(id+"F0.wireOp",EDGE,"E0.right")])],"isStart":false}),makeQuery(id+"F3.opExtrude","SWEPT_FACE",FACE,{"disambiguationData":[OSD([sQuery(id+"F2.wireOp",EDGE,"E5.bottom")])]}),makeQuery(id+"F3.opExtrude","SWEPT_FACE",FACE,{"disambiguationData":[OSD([sQuery(id+"F2.wireOp",EDGE,"E6.bottom")])]}),makeQuery(id+"F3.opExtrude","SWEPT_FACE",FACE,{"disambiguationData":[OSD([sQuery(id+"F2.wireOp",EDGE,"E7.bottom")])]})]}),makeQuery(id+"F5.opExtrude","SWEPT_FACE",FACE,{"disambiguationData":[OSD([sQuery(id+"F4.wireOp",EDGE,"E11.bottom")])]}),makeQuery(id+"F5.opExtrude","SWEPT_FACE",FACE,{"disambiguationData":[OSD([sQuery(id+"F4.wireOp",EDGE,"E12.bottom")])]}),makeQuery(id+"F5.opExtrude","SWEPT_FACE",FACE,{"disambiguationData":[OSD([sQuery(id+"F4.wireOp",EDGE,"E13.bottom")])]})]}),makeQuery(id+"F7.opExtrude","SWEPT_FACE",FACE,{"disambiguationData":[OSD([sQuery(id+"F6.wireOp",EDGE,"E19.2.0.0")])]})]});
            var Q19;
            Q19=makeQuery(id+"F7.boolean.opBoolean","INTERSECT",EDGE,{"derivedFrom":[makeQuery(id+"F5.boolean.opBoolean","MERGE",FACE,{"derivedFrom":[makeQuery(id+"F3.boolean.opBoolean","MERGE",FACE,{"derivedFrom":[makeQuery(id+"F1.opExtrude","CAP_FACE",FACE,{"disambiguationData":[OSD([sQuery(id+"F0.wireOp",EDGE,"E0.bottom"),sQuery(id+"F0.wireOp",EDGE,"E0.top"),sQuery(id+"F0.wireOp",EDGE,"E0.left"),sQuery(id+"F0.wireOp",EDGE,"E0.right")])],"isStart":false}),makeQuery(id+"F3.opExtrude","SWEPT_FACE",FACE,{"disambiguationData":[OSD([sQuery(id+"F2.wireOp",EDGE,"E5.bottom")])]}),makeQuery(id+"F3.opExtrude","SWEPT_FACE",FACE,{"disambiguationData":[OSD([sQuery(id+"F2.wireOp",EDGE,"E6.bottom")])]}),makeQuery(id+"F3.opExtrude","SWEPT_FACE",FACE,{"disambiguationData":[OSD([sQuery(id+"F2.wireOp",EDGE,"E7.bottom")])]})]}),makeQuery(id+"F5.opExtrude","SWEPT_FACE",FACE,{"disambiguationData":[OSD([sQuery(id+"F4.wireOp",EDGE,"E11.bottom")])]}),makeQuery(id+"F5.opExtrude","SWEPT_FACE",FACE,{"disambiguationData":[OSD([sQuery(id+"F4.wireOp",EDGE,"E12.bottom")])]}),makeQuery(id+"F5.opExtrude","SWEPT_FACE",FACE,{"disambiguationData":[OSD([sQuery(id+"F4.wireOp",EDGE,"E13.bottom")])]})]}),makeQuery(id+"F7.opExtrude","SWEPT_FACE",FACE,{"disambiguationData":[OSD([sQuery(id+"F6.wireOp",EDGE,"E19.3.0.0")])]})]});
            var Q20;
            Q20=makeQuery(id+"F7.boolean.opBoolean","INTERSECT",EDGE,{"derivedFrom":[makeQuery(id+"F5.boolean.opBoolean","MERGE",FACE,{"derivedFrom":[makeQuery(id+"F3.boolean.opBoolean","MERGE",FACE,{"derivedFrom":[makeQuery(id+"F1.opExtrude","CAP_FACE",FACE,{"disambiguationData":[OSD([sQuery(id+"F0.wireOp",EDGE,"E0.bottom"),sQuery(id+"F0.wireOp",EDGE,"E0.top"),sQuery(id+"F0.wireOp",EDGE,"E0.left"),sQuery(id+"F0.wireOp",EDGE,"E0.right")])],"isStart":false}),makeQuery(id+"F3.opExtrude","SWEPT_FACE",FACE,{"disambiguationData":[OSD([sQuery(id+"F2.wireOp",EDGE,"E5.bottom")])]}),makeQuery(id+"F3.opExtrude","SWEPT_FACE",FACE,{"disambiguationData":[OSD([sQuery(id+"F2.wireOp",EDGE,"E6.bottom")])]}),makeQuery(id+"F3.opExtrude","SWEPT_FACE",FACE,{"disambiguationData":[OSD([sQuery(id+"F2.wireOp",EDGE,"E7.bottom")])]})]}),makeQuery(id+"F5.opExtrude","SWEPT_FACE",FACE,{"disambiguationData":[OSD([sQuery(id+"F4.wireOp",EDGE,"E11.bottom")])]}),makeQuery(id+"F5.opExtrude","SWEPT_FACE",FACE,{"disambiguationData":[OSD([sQuery(id+"F4.wireOp",EDGE,"E12.bottom")])]}),makeQuery(id+"F5.opExtrude","SWEPT_FACE",FACE,{"disambiguationData":[OSD([sQuery(id+"F4.wireOp",EDGE,"E13.bottom")])]})]}),makeQuery(id+"F7.opExtrude","SWEPT_FACE",FACE,{"disambiguationData":[OSD([sQuery(id+"F6.wireOp",EDGE,"E19.4.0.0")])]})]});
            var Q21;
            Q21=makeQuery(id+"F7.boolean.opBoolean","INTERSECT",EDGE,{"derivedFrom":[makeQuery(id+"F5.boolean.opBoolean","MERGE",FACE,{"derivedFrom":[makeQuery(id+"F3.boolean.opBoolean","MERGE",FACE,{"derivedFrom":[makeQuery(id+"F1.opExtrude","CAP_FACE",FACE,{"disambiguationData":[OSD([sQuery(id+"F0.wireOp",EDGE,"E0.bottom"),sQuery(id+"F0.wireOp",EDGE,"E0.top"),sQuery(id+"F0.wireOp",EDGE,"E0.left"),sQuery(id+"F0.wireOp",EDGE,"E0.right")])],"isStart":false}),makeQuery(id+"F3.opExtrude","SWEPT_FACE",FACE,{"disambiguationData":[OSD([sQuery(id+"F2.wireOp",EDGE,"E5.bottom")])]}),makeQuery(id+"F3.opExtrude","SWEPT_FACE",FACE,{"disambiguationData":[OSD([sQuery(id+"F2.wireOp",EDGE,"E6.bottom")])]}),makeQuery(id+"F3.opExtrude","SWEPT_FACE",FACE,{"disambiguationData":[OSD([sQuery(id+"F2.wireOp",EDGE,"E7.bottom")])]})]}),makeQuery(id+"F5.opExtrude","SWEPT_FACE",FACE,{"disambiguationData":[OSD([sQuery(id+"F4.wireOp",EDGE,"E11.bottom")])]}),makeQuery(id+"F5.opExtrude","SWEPT_FACE",FACE,{"disambiguationData":[OSD([sQuery(id+"F4.wireOp",EDGE,"E12.bottom")])]}),makeQuery(id+"F5.opExtrude","SWEPT_FACE",FACE,{"disambiguationData":[OSD([sQuery(id+"F4.wireOp",EDGE,"E13.bottom")])]})]}),makeQuery(id+"F7.opExtrude","SWEPT_FACE",FACE,{"disambiguationData":[OSD([sQuery(id+"F6.wireOp",EDGE,"E19.5.0.0")])]})]});
            var Q22;
            Q22=makeQuery(id+"F7.boolean.opBoolean","INTERSECT",EDGE,{"derivedFrom":[makeQuery(id+"F5.boolean.opBoolean","MERGE",FACE,{"derivedFrom":[makeQuery(id+"F3.boolean.opBoolean","MERGE",FACE,{"derivedFrom":[makeQuery(id+"F1.opExtrude","CAP_FACE",FACE,{"disambiguationData":[OSD([sQuery(id+"F0.wireOp",EDGE,"E0.bottom"),sQuery(id+"F0.wireOp",EDGE,"E0.top"),sQuery(id+"F0.wireOp",EDGE,"E0.left"),sQuery(id+"F0.wireOp",EDGE,"E0.right")])],"isStart":false}),makeQuery(id+"F3.opExtrude","SWEPT_FACE",FACE,{"disambiguationData":[OSD([sQuery(id+"F2.wireOp",EDGE,"E5.bottom")])]}),makeQuery(id+"F3.opExtrude","SWEPT_FACE",FACE,{"disambiguationData":[OSD([sQuery(id+"F2.wireOp",EDGE,"E6.bottom")])]}),makeQuery(id+"F3.opExtrude","SWEPT_FACE",FACE,{"disambiguationData":[OSD([sQuery(id+"F2.wireOp",EDGE,"E7.bottom")])]})]}),makeQuery(id+"F5.opExtrude","SWEPT_FACE",FACE,{"disambiguationData":[OSD([sQuery(id+"F4.wireOp",EDGE,"E11.bottom")])]}),makeQuery(id+"F5.opExtrude","SWEPT_FACE",FACE,{"disambiguationData":[OSD([sQuery(id+"F4.wireOp",EDGE,"E12.bottom")])]}),makeQuery(id+"F5.opExtrude","SWEPT_FACE",FACE,{"disambiguationData":[OSD([sQuery(id+"F4.wireOp",EDGE,"E13.bottom")])]})]}),makeQuery(id+"F7.opExtrude","SWEPT_FACE",FACE,{"disambiguationData":[OSD([sQuery(id+"F6.wireOp",EDGE,"E19.6.0.0")])]})]});
            var Q23;
            Q23=makeQuery(id+"F7.boolean.opBoolean","INTERSECT",EDGE,{"derivedFrom":[makeQuery(id+"F5.boolean.opBoolean","MERGE",FACE,{"derivedFrom":[makeQuery(id+"F3.boolean.opBoolean","MERGE",FACE,{"derivedFrom":[makeQuery(id+"F1.opExtrude","CAP_FACE",FACE,{"disambiguationData":[OSD([sQuery(id+"F0.wireOp",EDGE,"E0.bottom"),sQuery(id+"F0.wireOp",EDGE,"E0.top"),sQuery(id+"F0.wireOp",EDGE,"E0.left"),sQuery(id+"F0.wireOp",EDGE,"E0.right")])],"isStart":false}),makeQuery(id+"F3.opExtrude","SWEPT_FACE",FACE,{"disambiguationData":[OSD([sQuery(id+"F2.wireOp",EDGE,"E5.bottom")])]}),makeQuery(id+"F3.opExtrude","SWEPT_FACE",FACE,{"disambiguationData":[OSD([sQuery(id+"F2.wireOp",EDGE,"E6.bottom")])]}),makeQuery(id+"F3.opExtrude","SWEPT_FACE",FACE,{"disambiguationData":[OSD([sQuery(id+"F2.wireOp",EDGE,"E7.bottom")])]})]}),makeQuery(id+"F5.opExtrude","SWEPT_FACE",FACE,{"disambiguationData":[OSD([sQuery(id+"F4.wireOp",EDGE,"E11.bottom")])]}),makeQuery(id+"F5.opExtrude","SWEPT_FACE",FACE,{"disambiguationData":[OSD([sQuery(id+"F4.wireOp",EDGE,"E12.bottom")])]}),makeQuery(id+"F5.opExtrude","SWEPT_FACE",FACE,{"disambiguationData":[OSD([sQuery(id+"F4.wireOp",EDGE,"E13.bottom")])]})]}),makeQuery(id+"F7.opExtrude","SWEPT_FACE",FACE,{"disambiguationData":[OSD([sQuery(id+"F6.wireOp",EDGE,"E19.7.0.0")])]})]});
            fillet(context, id + "F9", {"entities" : qUnion([Q0, Q1, Q2, Q3, Q4, Q5, Q6, Q7, Q8, Q9, Q10, Q11, Q12, Q13, Q14, Q15, Q16, Q17, Q18, Q19, Q20, Q21, Q22, Q23]), "radius" : 5 * mm, "tangentPropagation" : true, "allowEdgeOverflow" : false});
        }
    });
